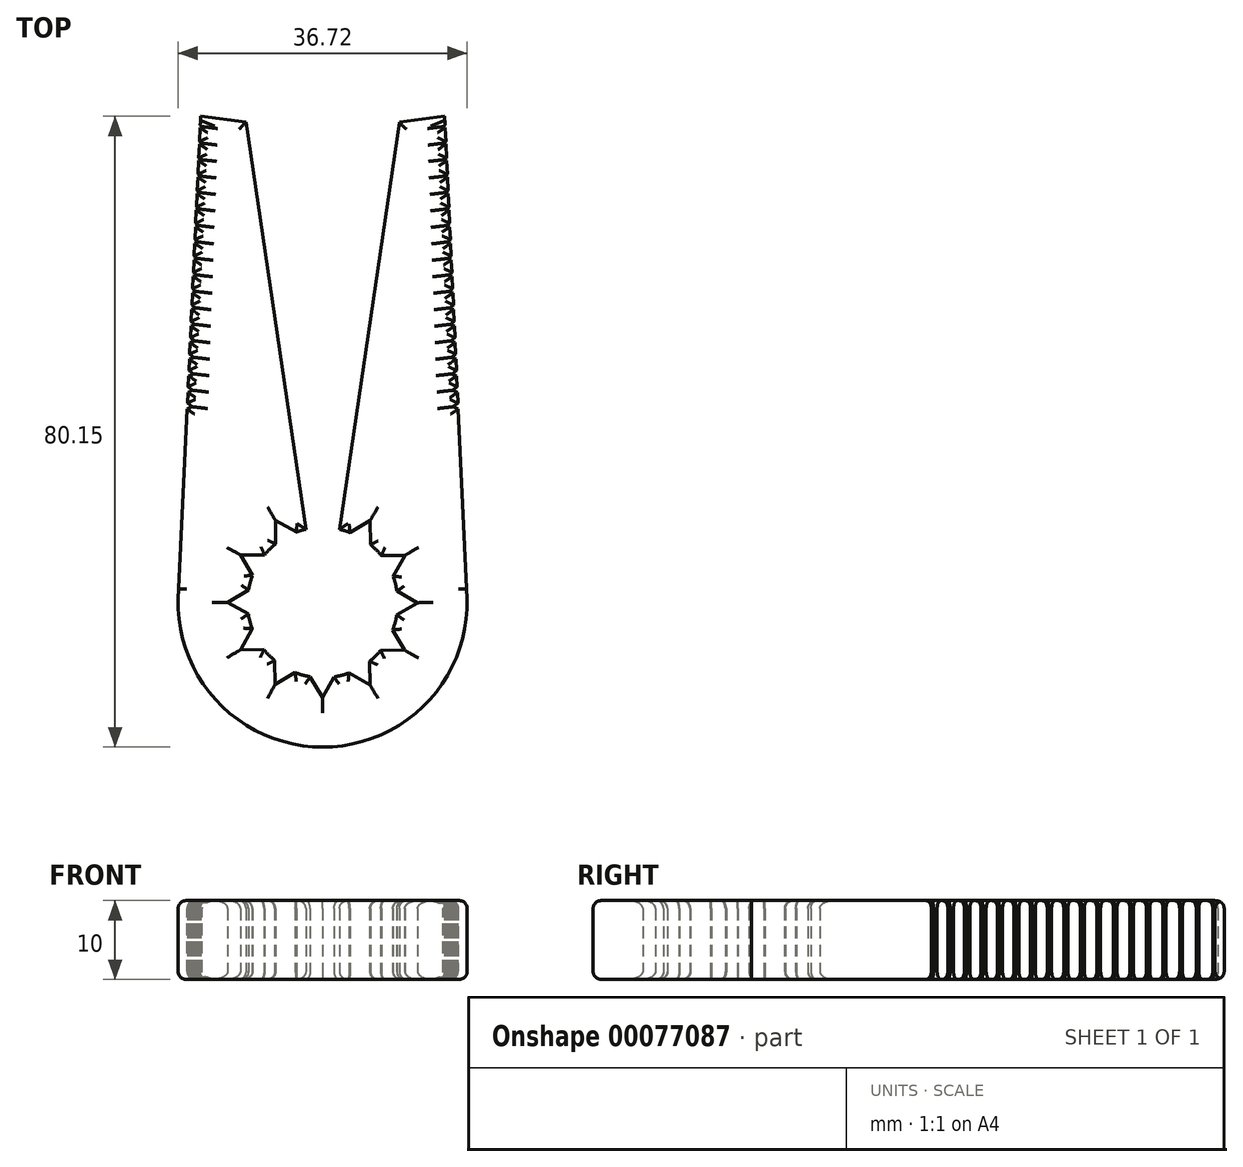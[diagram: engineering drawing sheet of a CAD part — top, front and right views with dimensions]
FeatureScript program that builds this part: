
annotation { "Feature Type Name" : "Feature", "Feature Type Description" : "" }
export const myFeature = defineFeature(function(context is Context, id is Id, definition is map)
    precondition{}
    {
        {
            var Q0;
            Q0=qCreatedBy(makeId("Top.planeOp"),FACE);
            var sketch = newSketch(context, id + "F0", { "sketchPlane" : qUnion([Q0])});
            skLineSegment(sketch, "E0", {"start": v(-9.75, 60.98) * mm, "end": v(-15.5, 61.76) * mm});
            skLineSegment(sketch, "E1", {"start": v(-15.5, 61.76) * mm, "end": v(-16.2, 46.6) * mm});
            skLineSegment(sketch, "E2", {"start": v(0, 52.98) * mm, "end": v(0, 8.77) * mm, "construction": true});
            skArc(sketch, "E3.trimOffspring", {"start": v(-18.28, 1.74) * mm, "mid": v(-13.6, -12.37) * mm, "end": v(0, -18.4) * mm});
            skArc(sketch, "E4.MirrorCS", {"start": v(18.28, 1.74) * mm, "mid": v(13.6, -12.37) * mm, "end": v(0, -18.4) * mm});
            skLineSegment(sketch, "E5.MirrorCS", {"start": v(15.5, 61.76) * mm, "end": v(16.2, 46.6) * mm});
            skLineSegment(sketch, "E6.MirrorCS", {"start": v(9.75, 60.98) * mm, "end": v(15.5, 61.76) * mm});
            skLineSegment(sketch, "E7.MirrorCS", {"start": v(2.13, 9.28) * mm, "end": v(9.75, 60.98) * mm});
            skLineSegment(sketch, "E8.trimOffspring", {"start": v(-16.76, 34.47) * mm, "end": v(-18.28, 1.74) * mm});
            skLineSegment(sketch, "E9.trimOffspring", {"start": v(16.76, 34.47) * mm, "end": v(18.28, 1.74) * mm});
            skLineSegment(sketch, "E10", {"start": v(-2.13, 9.28) * mm, "end": v(-9.75, 60.98) * mm});
            skLineSegment(sketch, "E11.trimOffspring", {"start": v(0, 8.03) * mm, "end": v(0, -53.52) * mm, "construction": true});
            skArc(sketch, "E12", {"start": v(-2.13, 9.28) * mm, "mid": v(-2.74, 9.12) * mm, "end": v(-3.34, 8.92) * mm});
            skLineSegment(sketch, "E13", {"start": v(0, -0.03) * mm, "end": v(-26.83, -0.03) * mm, "construction": true});
            skArc(sketch, "E14.cCircle", {"start": v(-7.66, -0.03) * mm, "mid": v(-7.66, 0) * mm, "end": v(-7.66, 0.04) * mm, "construction": true});
            skLineSegment(sketch, "E14.0", {"start": v(-12.05, 0) * mm, "end": v(-9.42, 1.55) * mm});
            skLineSegment(sketch, "E14.1", {"start": v(-7.66, 0.04) * mm, "end": v(-7.66, -0.03) * mm});
            skLineSegment(sketch, "E14.2", {"start": v(-9.44, -1.47) * mm, "end": v(-12.05, 0) * mm});
            skPoint(sketch, "E14.0.midPoint", {"position": v(-9.87, 1.28) * mm});
            skPoint(sketch, "E15.orphan", {"position": v(-7.69, 2.57) * mm});
            skPoint(sketch, "E16.orphan", {"position": v(-7.63, -2.49) * mm});
            skPoint(sketch, "E17.1.0", {"position": v(-9.2, -3.83) * mm});
            skLineSegment(sketch, "E17.1.1", {"start": v(-10.44, -6.03) * mm, "end": v(-8.95, -3.37) * mm});
            skLineSegment(sketch, "E17.1.2", {"start": v(-7.45, -6) * mm, "end": v(-10.44, -6.03) * mm});
            skPoint(sketch, "E17.2.0", {"position": v(-6.07, -7.92) * mm});
            skLineSegment(sketch, "E17.2.1", {"start": v(-6.04, -10.45) * mm, "end": v(-6.08, -7.4) * mm});
            skLineSegment(sketch, "E17.2.2", {"start": v(-3.47, -8.93) * mm, "end": v(-6.04, -10.45) * mm});
            skPoint(sketch, "E17.3.0", {"position": v(-1.31, -9.9) * mm});
            skLineSegment(sketch, "E17.3.1", {"start": v(-0.02, -12.08) * mm, "end": v(-1.58, -9.45) * mm});
            skLineSegment(sketch, "E17.3.2", {"start": v(1.44, -9.47) * mm, "end": v(-0.02, -12.08) * mm});
            skPoint(sketch, "E17.4.0", {"position": v(3.8, -9.23) * mm});
            skLineSegment(sketch, "E17.4.1", {"start": v(6, -10.47) * mm, "end": v(3.34, -8.97) * mm});
            skLineSegment(sketch, "E17.4.2", {"start": v(5.97, -7.48) * mm, "end": v(6, -10.47) * mm});
            skPoint(sketch, "E17.5.0", {"position": v(7.9, -6.1) * mm});
            skLineSegment(sketch, "E17.5.1", {"start": v(10.42, -6.07) * mm, "end": v(7.37, -6.1) * mm});
            skLineSegment(sketch, "E17.5.2", {"start": v(8.9, -3.5) * mm, "end": v(10.42, -6.07) * mm});
            skPoint(sketch, "E17.6.0", {"position": v(9.87, -1.34) * mm});
            skLineSegment(sketch, "E17.6.1", {"start": v(12.05, -0.05) * mm, "end": v(9.42, -1.6) * mm});
            skLineSegment(sketch, "E17.6.2", {"start": v(9.44, 1.42) * mm, "end": v(12.05, -0.05) * mm});
            skPoint(sketch, "E17.7.0", {"position": v(9.2, 3.77) * mm});
            skLineSegment(sketch, "E17.7.1", {"start": v(10.44, 5.98) * mm, "end": v(8.95, 3.31) * mm});
            skLineSegment(sketch, "E17.7.2", {"start": v(7.45, 5.94) * mm, "end": v(10.44, 5.98) * mm});
            skPoint(sketch, "E17.8.0", {"position": v(6.07, 7.86) * mm});
            skLineSegment(sketch, "E17.8.1", {"start": v(6.04, 10.4) * mm, "end": v(6.08, 7.34) * mm});
            skLineSegment(sketch, "E17.8.2", {"start": v(3.47, 8.87) * mm, "end": v(6.04, 10.4) * mm});
            skPoint(sketch, "E17.9.0", {"position": v(1.31, 9.84) * mm});
            skLineSegment(sketch, "E17.9.1", {"start": v(0, 12.05) * mm, "end": v(0.02, 12.02) * mm});
            skPoint(sketch, "E17.10.0", {"position": v(-3.8, 9.17) * mm});
            skLineSegment(sketch, "E17.10.1", {"start": v(-6, 10.42) * mm, "end": v(-3.34, 8.92) * mm});
            skLineSegment(sketch, "E17.10.2", {"start": v(-5.97, 7.42) * mm, "end": v(-6, 10.42) * mm});
            skPoint(sketch, "E17.11.0", {"position": v(-7.9, 6.04) * mm});
            skLineSegment(sketch, "E17.11.1", {"start": v(-10.42, 6.01) * mm, "end": v(-7.37, 6.05) * mm});
            skLineSegment(sketch, "E17.11.2", {"start": v(-8.9, 3.44) * mm, "end": v(-10.42, 6.01) * mm});
            skArc(sketch, "E18.trimOffspring", {"start": v(3.47, 8.87) * mm, "mid": v(2.8, 9.1) * mm, "end": v(2.13, 9.28) * mm});
            skArc(sketch, "E19.trimOffspring", {"start": v(7.45, 5.94) * mm, "mid": v(6.8, 6.68) * mm, "end": v(6.08, 7.34) * mm});
            skArc(sketch, "E20.trimOffspring", {"start": v(9.44, 1.42) * mm, "mid": v(9.24, 2.38) * mm, "end": v(8.95, 3.31) * mm});
            skArc(sketch, "E21.trimOffspring", {"start": v(8.9, -3.5) * mm, "mid": v(9.2, -2.57) * mm, "end": v(9.42, -1.6) * mm});
            skArc(sketch, "E22.trimOffspring", {"start": v(5.97, -7.48) * mm, "mid": v(6.7, -6.83) * mm, "end": v(7.37, -6.1) * mm});
            skArc(sketch, "E23.trimOffspring", {"start": v(1.44, -9.47) * mm, "mid": v(2.4, -9.27) * mm, "end": v(3.34, -8.97) * mm});
            skArc(sketch, "E24.trimOffspring", {"start": v(-3.47, -8.93) * mm, "mid": v(-2.54, -9.24) * mm, "end": v(-1.58, -9.45) * mm});
            skArc(sketch, "E25.trimOffspring", {"start": v(-7.45, -6) * mm, "mid": v(-6.8, -6.73) * mm, "end": v(-6.08, -7.4) * mm});
            skArc(sketch, "E26.trimOffspring", {"start": v(-9.44, -1.47) * mm, "mid": v(-9.24, -2.43) * mm, "end": v(-8.95, -3.37) * mm});
            skArc(sketch, "E27.trimOffspring", {"start": v(-8.9, 3.44) * mm, "mid": v(-9.2, 2.5) * mm, "end": v(-9.42, 1.55) * mm});
            skArc(sketch, "E28.trimOffspring", {"start": v(-5.97, 7.42) * mm, "mid": v(-6.7, 6.77) * mm, "end": v(-7.37, 6.05) * mm});
            skLineSegment(sketch, "E29", {"start": v(-16.2, 46.6) * mm, "end": v(-16.76, 34.47) * mm});
            skLineSegment(sketch, "E30", {"start": v(16.2, 46.6) * mm, "end": v(16.76, 34.47) * mm});
            skSolve(sketch);
        }
        {
            var Q0;
            Q0=makeQuery(id+"F0.imprint","IMPRINT",FACE,{"disambiguationData":[TD([[makeQuery(id+"F0.imprint","IMPRINT",EDGE,{"derivedFrom":sQuery(id+"F0.wireOp",EDGE,"E0")}),1.0]])]});
            extrude(context, id + "F1", {"entities" : qUnion([Q0]), "depth" : 10 * mm});
        }
        {
            var Q0;
            Q0=qCreatedBy(makeId("Top.planeOp"),FACE);
            var sketch = newSketch(context, id + "F2", { "sketchPlane" : qUnion([Q0])});
            skLineSegment(sketch, "E31.0", {"start": v(-16.57, 24.85) * mm, "end": v(-25.04, 21.22) * mm});
            skLineSegment(sketch, "E31.1", {"start": v(-25.04, 21.22) * mm, "end": v(-23.95, 30.36) * mm});
            skLineSegment(sketch, "E31.2", {"start": v(-23.95, 30.36) * mm, "end": v(-16.57, 24.85) * mm});
            skPoint(sketch, "E31.0.midPoint", {"position": v(-20.8, 23.03) * mm});
            skLineSegment(sketch, "E32.1.0.0", {"start": v(-24.96, 23.31) * mm, "end": v(-23.87, 32.46) * mm});
            skPoint(sketch, "E32.1.0.1", {"position": v(-20.73, 25.13) * mm});
            skLineSegment(sketch, "E32.1.0.2", {"start": v(-23.87, 32.46) * mm, "end": v(-16.5, 26.94) * mm});
            skLineSegment(sketch, "E32.1.0.3", {"start": v(-16.5, 26.94) * mm, "end": v(-24.96, 23.31) * mm});
            skLineSegment(sketch, "E32.2.0.0", {"start": v(-24.89, 25.4) * mm, "end": v(-23.8, 34.55) * mm});
            skPoint(sketch, "E32.2.0.1", {"position": v(-20.66, 27.22) * mm});
            skLineSegment(sketch, "E32.2.0.2", {"start": v(-23.8, 34.55) * mm, "end": v(-16.42, 29.03) * mm});
            skLineSegment(sketch, "E32.2.0.3", {"start": v(-16.42, 29.03) * mm, "end": v(-24.89, 25.4) * mm});
            skLineSegment(sketch, "E32.3.0.0", {"start": v(-24.81, 27.5) * mm, "end": v(-23.72, 36.64) * mm});
            skPoint(sketch, "E32.3.0.1", {"position": v(-20.58, 29.31) * mm});
            skLineSegment(sketch, "E32.3.0.2", {"start": v(-23.72, 36.64) * mm, "end": v(-16.35, 31.13) * mm});
            skLineSegment(sketch, "E32.3.0.3", {"start": v(-16.35, 31.13) * mm, "end": v(-24.81, 27.5) * mm});
            skLineSegment(sketch, "E32.4.0.0", {"start": v(-24.74, 29.6) * mm, "end": v(-23.65, 38.74) * mm});
            skPoint(sketch, "E32.4.0.1", {"position": v(-20.5, 31.4) * mm});
            skLineSegment(sketch, "E32.4.0.2", {"start": v(-23.65, 38.74) * mm, "end": v(-16.27, 33.22) * mm});
            skLineSegment(sketch, "E32.4.0.3", {"start": v(-16.27, 33.22) * mm, "end": v(-24.74, 29.6) * mm});
            skLineSegment(sketch, "E32.5.0.0", {"start": v(-24.66, 31.69) * mm, "end": v(-23.57, 40.83) * mm});
            skPoint(sketch, "E32.5.0.1", {"position": v(-20.43, 33.5) * mm});
            skLineSegment(sketch, "E32.5.0.2", {"start": v(-23.57, 40.83) * mm, "end": v(-16.2, 35.31) * mm});
            skLineSegment(sketch, "E32.5.0.3", {"start": v(-16.2, 35.31) * mm, "end": v(-24.66, 31.69) * mm});
            skLineSegment(sketch, "E32.6.0.0", {"start": v(-24.59, 33.78) * mm, "end": v(-23.5, 42.92) * mm});
            skPoint(sketch, "E32.6.0.1", {"position": v(-20.36, 35.6) * mm});
            skLineSegment(sketch, "E32.6.0.2", {"start": v(-23.5, 42.92) * mm, "end": v(-16.12, 37.4) * mm});
            skLineSegment(sketch, "E32.6.0.3", {"start": v(-16.12, 37.4) * mm, "end": v(-24.59, 33.78) * mm});
            skLineSegment(sketch, "E32.7.0.0", {"start": v(-24.51, 35.87) * mm, "end": v(-23.42, 45.02) * mm});
            skPoint(sketch, "E32.7.0.1", {"position": v(-20.28, 37.69) * mm});
            skLineSegment(sketch, "E32.7.0.2", {"start": v(-23.42, 45.02) * mm, "end": v(-16.05, 39.5) * mm});
            skLineSegment(sketch, "E32.7.0.3", {"start": v(-16.05, 39.5) * mm, "end": v(-24.51, 35.87) * mm});
            skLineSegment(sketch, "E32.8.0.0", {"start": v(-24.44, 37.97) * mm, "end": v(-23.35, 47.1) * mm});
            skPoint(sketch, "E32.8.0.1", {"position": v(-20.2, 39.78) * mm});
            skLineSegment(sketch, "E32.8.0.2", {"start": v(-23.35, 47.1) * mm, "end": v(-15.98, 41.6) * mm});
            skLineSegment(sketch, "E32.8.0.3", {"start": v(-15.98, 41.6) * mm, "end": v(-24.44, 37.97) * mm});
            skLineSegment(sketch, "E32.9.0.0", {"start": v(-24.36, 40.06) * mm, "end": v(-23.27, 49.2) * mm});
            skPoint(sketch, "E32.9.0.1", {"position": v(-20.13, 41.87) * mm});
            skLineSegment(sketch, "E32.9.0.2", {"start": v(-23.27, 49.2) * mm, "end": v(-15.9, 43.69) * mm});
            skLineSegment(sketch, "E32.9.0.3", {"start": v(-15.9, 43.69) * mm, "end": v(-24.36, 40.06) * mm});
            skLineSegment(sketch, "E32.10.0.0", {"start": v(-24.29, 42.15) * mm, "end": v(-23.2, 51.3) * mm});
            skPoint(sketch, "E32.10.0.1", {"position": v(-20.06, 43.97) * mm});
            skLineSegment(sketch, "E32.10.0.2", {"start": v(-23.2, 51.3) * mm, "end": v(-15.83, 45.78) * mm});
            skLineSegment(sketch, "E32.10.0.3", {"start": v(-15.83, 45.78) * mm, "end": v(-24.29, 42.15) * mm});
            skLineSegment(sketch, "E32.11.0.0", {"start": v(-24.21, 44.25) * mm, "end": v(-23.12, 53.39) * mm});
            skPoint(sketch, "E32.11.0.1", {"position": v(-19.98, 46.06) * mm});
            skLineSegment(sketch, "E32.11.0.2", {"start": v(-23.12, 53.39) * mm, "end": v(-15.75, 47.87) * mm});
            skLineSegment(sketch, "E32.11.0.3", {"start": v(-15.75, 47.87) * mm, "end": v(-24.21, 44.25) * mm});
            skLineSegment(sketch, "E32.12.0.0", {"start": v(-24.14, 46.34) * mm, "end": v(-23.05, 55.48) * mm});
            skPoint(sketch, "E32.12.0.1", {"position": v(-19.9, 48.15) * mm});
            skLineSegment(sketch, "E32.12.0.2", {"start": v(-23.05, 55.48) * mm, "end": v(-15.68, 49.97) * mm});
            skLineSegment(sketch, "E32.12.0.3", {"start": v(-15.68, 49.97) * mm, "end": v(-24.14, 46.34) * mm});
            skLineSegment(sketch, "E32.13.0.0", {"start": v(-24.06, 48.43) * mm, "end": v(-22.97, 57.57) * mm});
            skPoint(sketch, "E32.13.0.1", {"position": v(-19.83, 50.25) * mm});
            skLineSegment(sketch, "E32.13.0.2", {"start": v(-22.97, 57.57) * mm, "end": v(-15.6, 52.06) * mm});
            skLineSegment(sketch, "E32.13.0.3", {"start": v(-15.6, 52.06) * mm, "end": v(-24.06, 48.43) * mm});
            skLineSegment(sketch, "E32.14.0.0", {"start": v(-23.99, 50.53) * mm, "end": v(-22.9, 59.67) * mm});
            skPoint(sketch, "E32.14.0.1", {"position": v(-19.76, 52.34) * mm});
            skLineSegment(sketch, "E32.14.0.2", {"start": v(-22.9, 59.67) * mm, "end": v(-15.53, 54.15) * mm});
            skLineSegment(sketch, "E32.14.0.3", {"start": v(-15.53, 54.15) * mm, "end": v(-23.99, 50.53) * mm});
            skLineSegment(sketch, "E32.15.0.0", {"start": v(-23.91, 52.62) * mm, "end": v(-22.82, 61.76) * mm});
            skPoint(sketch, "E32.15.0.1", {"position": v(-19.68, 54.43) * mm});
            skLineSegment(sketch, "E32.15.0.2", {"start": v(-22.82, 61.76) * mm, "end": v(-15.45, 56.25) * mm});
            skLineSegment(sketch, "E32.15.0.3", {"start": v(-15.45, 56.25) * mm, "end": v(-23.91, 52.62) * mm});
            skLineSegment(sketch, "E32.16.0.0", {"start": v(-23.84, 54.71) * mm, "end": v(-22.75, 63.85) * mm});
            skPoint(sketch, "E32.16.0.1", {"position": v(-19.6, 56.53) * mm});
            skLineSegment(sketch, "E32.16.0.2", {"start": v(-22.75, 63.85) * mm, "end": v(-15.38, 58.34) * mm});
            skLineSegment(sketch, "E32.16.0.3", {"start": v(-15.38, 58.34) * mm, "end": v(-23.84, 54.71) * mm});
            skLineSegment(sketch, "E32.17.0.0", {"start": v(-23.76, 56.8) * mm, "end": v(-22.67, 65.95) * mm});
            skPoint(sketch, "E32.17.0.1", {"position": v(-19.53, 58.62) * mm});
            skLineSegment(sketch, "E32.17.0.2", {"start": v(-22.67, 65.95) * mm, "end": v(-15.3, 60.43) * mm});
            skLineSegment(sketch, "E32.17.0.3", {"start": v(-15.3, 60.43) * mm, "end": v(-23.76, 56.8) * mm});
            skLineSegment(sketch, "E32.direction1", {"start": v(-25.04, 21.22) * mm, "end": v(-24.96, 23.31) * mm, "construction": true});
            skLineSegment(sketch, "E33", {"start": v(0, 70.25) * mm, "end": v(0, -30.92) * mm, "construction": true});
            skLineSegment(sketch, "E34.MirrorCS", {"start": v(25.04, 21.22) * mm, "end": v(24.96, 23.31) * mm, "construction": true});
            skLineSegment(sketch, "E35.MirrorCS", {"start": v(24.36, 40.06) * mm, "end": v(23.27, 49.2) * mm});
            skLineSegment(sketch, "E36.MirrorCS", {"start": v(24.51, 35.87) * mm, "end": v(23.42, 45.02) * mm});
            skLineSegment(sketch, "E37.MirrorCS", {"start": v(23.76, 56.8) * mm, "end": v(22.67, 65.95) * mm});
            skLineSegment(sketch, "E38.MirrorCS", {"start": v(24.66, 31.69) * mm, "end": v(23.57, 40.83) * mm});
            skLineSegment(sketch, "E39.MirrorCS", {"start": v(24.44, 37.97) * mm, "end": v(23.35, 47.1) * mm});
            skLineSegment(sketch, "E40.MirrorCS", {"start": v(25.04, 21.22) * mm, "end": v(23.95, 30.36) * mm});
            skLineSegment(sketch, "E41.MirrorCS", {"start": v(23.99, 50.53) * mm, "end": v(22.9, 59.67) * mm});
            skLineSegment(sketch, "E42.MirrorCS", {"start": v(24.81, 27.5) * mm, "end": v(23.72, 36.64) * mm});
            skLineSegment(sketch, "E43.MirrorCS", {"start": v(24.29, 42.15) * mm, "end": v(23.2, 51.3) * mm});
            skLineSegment(sketch, "E44.MirrorCS", {"start": v(24.21, 44.25) * mm, "end": v(23.12, 53.39) * mm});
            skLineSegment(sketch, "E45.MirrorCS", {"start": v(24.89, 25.4) * mm, "end": v(23.8, 34.55) * mm});
            skLineSegment(sketch, "E46.MirrorCS", {"start": v(23.84, 54.71) * mm, "end": v(22.75, 63.85) * mm});
            skLineSegment(sketch, "E47.MirrorCS", {"start": v(24.14, 46.34) * mm, "end": v(23.05, 55.48) * mm});
            skLineSegment(sketch, "E48.MirrorCS", {"start": v(24.96, 23.31) * mm, "end": v(23.87, 32.46) * mm});
            skLineSegment(sketch, "E49.MirrorCS", {"start": v(24.59, 33.78) * mm, "end": v(23.5, 42.92) * mm});
            skLineSegment(sketch, "E50.MirrorCS", {"start": v(23.91, 52.62) * mm, "end": v(22.82, 61.76) * mm});
            skLineSegment(sketch, "E51.MirrorCS", {"start": v(24.74, 29.6) * mm, "end": v(23.65, 38.74) * mm});
            skLineSegment(sketch, "E52.MirrorCS", {"start": v(24.06, 48.43) * mm, "end": v(22.97, 57.57) * mm});
            skLineSegment(sketch, "E53.MirrorCS", {"start": v(22.9, 59.67) * mm, "end": v(15.53, 54.15) * mm});
            skLineSegment(sketch, "E54.MirrorCS", {"start": v(23.95, 30.36) * mm, "end": v(16.57, 24.85) * mm});
            skLineSegment(sketch, "E55.MirrorCS", {"start": v(15.53, 54.15) * mm, "end": v(23.99, 50.53) * mm});
            skLineSegment(sketch, "E56.MirrorCS", {"start": v(16.27, 33.22) * mm, "end": v(24.74, 29.6) * mm});
            skLineSegment(sketch, "E57.MirrorCS", {"start": v(23.57, 40.83) * mm, "end": v(16.2, 35.31) * mm});
            skLineSegment(sketch, "E58.MirrorCS", {"start": v(23.42, 45.02) * mm, "end": v(16.05, 39.5) * mm});
            skLineSegment(sketch, "E59.MirrorCS", {"start": v(23.5, 42.92) * mm, "end": v(16.12, 37.4) * mm});
            skLineSegment(sketch, "E60.MirrorCS", {"start": v(23.12, 53.39) * mm, "end": v(15.75, 47.87) * mm});
            skLineSegment(sketch, "E61.MirrorCS", {"start": v(15.3, 60.43) * mm, "end": v(23.76, 56.8) * mm});
            skPoint(sketch, "E62.MirrorP", {"position": v(19.83, 50.25) * mm});
            skLineSegment(sketch, "E63.MirrorCS", {"start": v(23.05, 55.48) * mm, "end": v(15.68, 49.97) * mm});
            skPoint(sketch, "E64.MirrorP", {"position": v(20.43, 33.5) * mm});
            skLineSegment(sketch, "E65.MirrorCS", {"start": v(22.67, 65.95) * mm, "end": v(15.3, 60.43) * mm});
            skLineSegment(sketch, "E66.MirrorCS", {"start": v(16.12, 37.4) * mm, "end": v(24.59, 33.78) * mm});
            skLineSegment(sketch, "E67.MirrorCS", {"start": v(16.5, 26.94) * mm, "end": v(24.96, 23.31) * mm});
            skLineSegment(sketch, "E68.MirrorCS", {"start": v(23.87, 32.46) * mm, "end": v(16.5, 26.94) * mm});
            skLineSegment(sketch, "E69.MirrorCS", {"start": v(16.57, 24.85) * mm, "end": v(25.04, 21.22) * mm});
            skPoint(sketch, "E70.MirrorP", {"position": v(19.76, 52.34) * mm});
            skLineSegment(sketch, "E71.MirrorCS", {"start": v(23.27, 49.2) * mm, "end": v(15.9, 43.69) * mm});
            skLineSegment(sketch, "E72.MirrorCS", {"start": v(23.65, 38.74) * mm, "end": v(16.27, 33.22) * mm});
            skPoint(sketch, "E73.MirrorP", {"position": v(20.2, 39.78) * mm});
            skLineSegment(sketch, "E74.MirrorCS", {"start": v(22.97, 57.57) * mm, "end": v(15.6, 52.06) * mm});
            skPoint(sketch, "E75.MirrorP", {"position": v(20.28, 37.69) * mm});
            skPoint(sketch, "E76.MirrorP", {"position": v(20.36, 35.6) * mm});
            skLineSegment(sketch, "E77.MirrorCS", {"start": v(15.98, 41.6) * mm, "end": v(24.44, 37.97) * mm});
            skPoint(sketch, "E78.MirrorP", {"position": v(20.5, 31.4) * mm});
            skLineSegment(sketch, "E79.MirrorCS", {"start": v(16.35, 31.13) * mm, "end": v(24.81, 27.5) * mm});
            skPoint(sketch, "E80.MirrorP", {"position": v(20.58, 29.31) * mm});
            skLineSegment(sketch, "E81.MirrorCS", {"start": v(22.82, 61.76) * mm, "end": v(15.45, 56.25) * mm});
            skPoint(sketch, "E82.MirrorP", {"position": v(19.53, 58.62) * mm});
            skPoint(sketch, "E83.MirrorP", {"position": v(19.9, 48.15) * mm});
            skPoint(sketch, "E84.MirrorP", {"position": v(20.73, 25.13) * mm});
            skLineSegment(sketch, "E85.MirrorCS", {"start": v(16.2, 35.31) * mm, "end": v(24.66, 31.69) * mm});
            skLineSegment(sketch, "E86.MirrorCS", {"start": v(15.38, 58.34) * mm, "end": v(23.84, 54.71) * mm});
            skLineSegment(sketch, "E87.MirrorCS", {"start": v(23.72, 36.64) * mm, "end": v(16.35, 31.13) * mm});
            skPoint(sketch, "E88.MirrorP", {"position": v(19.68, 54.43) * mm});
            skLineSegment(sketch, "E89.MirrorCS", {"start": v(15.68, 49.97) * mm, "end": v(24.14, 46.34) * mm});
            skLineSegment(sketch, "E90.MirrorCS", {"start": v(23.2, 51.3) * mm, "end": v(15.83, 45.78) * mm});
            skPoint(sketch, "E91.MirrorP", {"position": v(19.6, 56.53) * mm});
            skPoint(sketch, "E92.MirrorP", {"position": v(20.8, 23.03) * mm});
            skLineSegment(sketch, "E93.MirrorCS", {"start": v(15.83, 45.78) * mm, "end": v(24.29, 42.15) * mm});
            skPoint(sketch, "E94.MirrorP", {"position": v(20.13, 41.87) * mm});
            skLineSegment(sketch, "E95.MirrorCS", {"start": v(16.42, 29.03) * mm, "end": v(24.89, 25.4) * mm});
            skLineSegment(sketch, "E96.MirrorCS", {"start": v(23.8, 34.55) * mm, "end": v(16.42, 29.03) * mm});
            skPoint(sketch, "E97.MirrorP", {"position": v(20.06, 43.97) * mm});
            skPoint(sketch, "E98.MirrorP", {"position": v(20.66, 27.22) * mm});
            skPoint(sketch, "E99.MirrorP", {"position": v(19.98, 46.06) * mm});
            skLineSegment(sketch, "E100.MirrorCS", {"start": v(15.9, 43.69) * mm, "end": v(24.36, 40.06) * mm});
            skLineSegment(sketch, "E101.MirrorCS", {"start": v(23.35, 47.1) * mm, "end": v(15.98, 41.6) * mm});
            skLineSegment(sketch, "E102.MirrorCS", {"start": v(15.45, 56.25) * mm, "end": v(23.91, 52.62) * mm});
            skLineSegment(sketch, "E103.MirrorCS", {"start": v(15.75, 47.87) * mm, "end": v(24.21, 44.25) * mm});
            skLineSegment(sketch, "E104.MirrorCS", {"start": v(22.75, 63.85) * mm, "end": v(15.38, 58.34) * mm});
            skLineSegment(sketch, "E105.MirrorCS", {"start": v(15.6, 52.06) * mm, "end": v(24.06, 48.43) * mm});
            skLineSegment(sketch, "E106.MirrorCS", {"start": v(16.05, 39.5) * mm, "end": v(24.51, 35.87) * mm});
            skSolve(sketch);
        }
        {
            var Q0;
            {var subQ5=sQuery(id+"F2.wireOp",EDGE,"E32.15.0.2");var subQ6=sQuery(id+"F2.wireOp",EDGE,"E32.15.0.0");var subQ7=makeQuery(id+"F2.imprint","INTERSECT",VERTEX,{"derivedFrom":[subQ6,subQ5]});Q0=makeQuery(id+"F2.imprint","IMPRINT",FACE,{"disambiguationData":[TD([[makeQuery(id+"F2.imprint","IMPRINT",EDGE,{"disambiguationData":[TD([[subQ7,1.0]])],"derivedFrom":subQ6}),1.0]])]});}
            var Q1;
            {var subQ0=sQuery(id+"F2.wireOp",EDGE,"E32.6.0.3");var subQ1=sQuery(id+"F2.wireOp",EDGE,"E32.5.0.2");var subQ2=makeQuery(id+"F2.imprint","INTERSECT",VERTEX,{"derivedFrom":[subQ1,subQ0]});Q1=makeQuery(id+"F2.imprint","IMPRINT",FACE,{"disambiguationData":[TD([[makeQuery(id+"F2.imprint","IMPRINT",EDGE,{"disambiguationData":[TD([[subQ2,1.0]])],"derivedFrom":subQ1}),1.0]])]});}
            var Q2;
            {var subQ0=sQuery(id+"F2.wireOp",EDGE,"E32.16.0.3");var subQ1=sQuery(id+"F2.wireOp",EDGE,"E32.15.0.2");var subQ2=makeQuery(id+"F2.imprint","INTERSECT",VERTEX,{"derivedFrom":[subQ1,subQ0]});Q2=makeQuery(id+"F2.imprint","IMPRINT",FACE,{"disambiguationData":[TD([[makeQuery(id+"F2.imprint","IMPRINT",EDGE,{"disambiguationData":[TD([[subQ2,1.0]])],"derivedFrom":subQ1}),1.0]])]});}
            var Q3;
            {var subQ0=sQuery(id+"F2.wireOp",EDGE,"E32.1.0.3");var subQ1=sQuery(id+"F2.wireOp",EDGE,"E31.1");var subQ2=makeQuery(id+"F2.imprint","INTERSECT",VERTEX,{"derivedFrom":[subQ1,subQ0]});Q3=makeQuery(id+"F2.imprint","IMPRINT",FACE,{"disambiguationData":[TD([[makeQuery(id+"F2.imprint","IMPRINT",EDGE,{"disambiguationData":[TD([[subQ2,-1.0]])],"derivedFrom":subQ1}),-1.0]])]});}
            var Q4;
            {var subQ0=sQuery(id+"F2.wireOp",EDGE,"E32.2.0.3");var subQ1=sQuery(id+"F2.wireOp",EDGE,"E31.1");var subQ2=makeQuery(id+"F2.imprint","INTERSECT",VERTEX,{"derivedFrom":[subQ1,subQ0]});Q4=makeQuery(id+"F2.imprint","IMPRINT",FACE,{"disambiguationData":[TD([[makeQuery(id+"F2.imprint","IMPRINT",EDGE,{"disambiguationData":[TD([[subQ2,-1.0]])],"derivedFrom":subQ1}),-1.0]])]});}
            var Q5;
            {var subQ0=sQuery(id+"F2.wireOp",EDGE,"E32.14.0.3");var subQ1=sQuery(id+"F2.wireOp",EDGE,"E32.13.0.2");var subQ2=makeQuery(id+"F2.imprint","INTERSECT",VERTEX,{"derivedFrom":[subQ1,subQ0]});Q5=makeQuery(id+"F2.imprint","IMPRINT",FACE,{"disambiguationData":[TD([[makeQuery(id+"F2.imprint","IMPRINT",EDGE,{"disambiguationData":[TD([[subQ2,1.0]])],"derivedFrom":subQ1}),1.0]])]});}
            var Q6;
            {var subQ0=sQuery(id+"F2.wireOp",EDGE,"E32.7.0.3");var subQ1=sQuery(id+"F2.wireOp",EDGE,"E32.6.0.2");var subQ2=makeQuery(id+"F2.imprint","INTERSECT",VERTEX,{"derivedFrom":[subQ1,subQ0]});Q6=makeQuery(id+"F2.imprint","IMPRINT",FACE,{"disambiguationData":[TD([[makeQuery(id+"F2.imprint","IMPRINT",EDGE,{"disambiguationData":[TD([[subQ2,1.0]])],"derivedFrom":subQ1}),1.0]])]});}
            var Q7;
            {var subQ0=sQuery(id+"F2.wireOp",EDGE,"E32.13.0.3");var subQ1=sQuery(id+"F2.wireOp",EDGE,"E32.12.0.2");var subQ2=makeQuery(id+"F2.imprint","INTERSECT",VERTEX,{"derivedFrom":[subQ1,subQ0]});Q7=makeQuery(id+"F2.imprint","IMPRINT",FACE,{"disambiguationData":[TD([[makeQuery(id+"F2.imprint","IMPRINT",EDGE,{"disambiguationData":[TD([[subQ2,1.0]])],"derivedFrom":subQ1}),1.0]])]});}
            var Q8;
            {var subQ0=sQuery(id+"F2.wireOp",EDGE,"E32.4.0.3");var subQ1=sQuery(id+"F2.wireOp",EDGE,"E32.3.0.2");var subQ2=makeQuery(id+"F2.imprint","INTERSECT",VERTEX,{"derivedFrom":[subQ1,subQ0]});Q8=makeQuery(id+"F2.imprint","IMPRINT",FACE,{"disambiguationData":[TD([[makeQuery(id+"F2.imprint","IMPRINT",EDGE,{"disambiguationData":[TD([[subQ2,1.0]])],"derivedFrom":subQ1}),1.0]])]});}
            var Q9;
            {var subQ1=sQuery(id+"F2.wireOp",EDGE,"E32.17.0.0");Q9=makeQuery(id+"F2.imprint","IMPRINT",FACE,{"disambiguationData":[TD([[makeQuery(id+"F2.imprint","IMPRINT",EDGE,{"derivedFrom":subQ1}),-1.0]])]});}
            var Q10;
            {var subQ0=sQuery(id+"F2.wireOp",EDGE,"E32.3.0.3");var subQ1=sQuery(id+"F2.wireOp",EDGE,"E32.2.0.2");var subQ2=makeQuery(id+"F2.imprint","INTERSECT",VERTEX,{"derivedFrom":[subQ1,subQ0]});Q10=makeQuery(id+"F2.imprint","IMPRINT",FACE,{"disambiguationData":[TD([[makeQuery(id+"F2.imprint","IMPRINT",EDGE,{"disambiguationData":[TD([[subQ2,1.0]])],"derivedFrom":subQ1}),1.0]])]});}
            var Q11;
            {var subQ0=sQuery(id+"F2.wireOp",EDGE,"E32.15.0.3");var subQ1=sQuery(id+"F2.wireOp",EDGE,"E32.14.0.2");var subQ2=makeQuery(id+"F2.imprint","INTERSECT",VERTEX,{"derivedFrom":[subQ1,subQ0]});Q11=makeQuery(id+"F2.imprint","IMPRINT",FACE,{"disambiguationData":[TD([[makeQuery(id+"F2.imprint","IMPRINT",EDGE,{"disambiguationData":[TD([[subQ2,1.0]])],"derivedFrom":subQ1}),1.0]])]});}
            var Q12;
            {var subQ0=sQuery(id+"F2.wireOp",EDGE,"E32.5.0.3");var subQ1=sQuery(id+"F2.wireOp",EDGE,"E32.4.0.2");var subQ2=makeQuery(id+"F2.imprint","INTERSECT",VERTEX,{"derivedFrom":[subQ1,subQ0]});Q12=makeQuery(id+"F2.imprint","IMPRINT",FACE,{"disambiguationData":[TD([[makeQuery(id+"F2.imprint","IMPRINT",EDGE,{"disambiguationData":[TD([[subQ2,1.0]])],"derivedFrom":subQ1}),1.0]])]});}
            var Q13;
            {var subQ0=sQuery(id+"F2.wireOp",EDGE,"E32.17.0.3");var subQ1=sQuery(id+"F2.wireOp",EDGE,"E32.14.0.2");var subQ2=makeQuery(id+"F2.imprint","INTERSECT",VERTEX,{"derivedFrom":[subQ1,subQ0]});Q13=makeQuery(id+"F2.imprint","IMPRINT",FACE,{"disambiguationData":[TD([[makeQuery(id+"F2.imprint","IMPRINT",EDGE,{"disambiguationData":[TD([[subQ2,-1.0]])],"derivedFrom":subQ1}),1.0]])]});}
            var Q14;
            {var subQ0=sQuery(id+"F2.wireOp",EDGE,"E32.13.0.3");var subQ1=sQuery(id+"F2.wireOp",EDGE,"E32.10.0.2");var subQ2=makeQuery(id+"F2.imprint","INTERSECT",VERTEX,{"derivedFrom":[subQ1,subQ0]});Q14=makeQuery(id+"F2.imprint","IMPRINT",FACE,{"disambiguationData":[TD([[makeQuery(id+"F2.imprint","IMPRINT",EDGE,{"disambiguationData":[TD([[subQ2,-1.0]])],"derivedFrom":subQ1}),1.0]])]});}
            var Q15;
            {var subQ0=sQuery(id+"F2.wireOp",EDGE,"E32.14.0.2");var subQ1=sQuery(id+"F2.wireOp",EDGE,"E32.14.0.0");var subQ2=makeQuery(id+"F2.imprint","INTERSECT",VERTEX,{"derivedFrom":[subQ1,subQ0]});Q15=makeQuery(id+"F2.imprint","IMPRINT",FACE,{"disambiguationData":[TD([[makeQuery(id+"F2.imprint","IMPRINT",EDGE,{"disambiguationData":[TD([[subQ2,1.0]])],"derivedFrom":subQ1}),1.0]])]});}
            var Q16;
            {var subQ0=sQuery(id+"F2.wireOp",EDGE,"E32.14.0.3");var subQ1=sQuery(id+"F2.wireOp",EDGE,"E32.10.0.2");var subQ2=makeQuery(id+"F2.imprint","INTERSECT",VERTEX,{"derivedFrom":[subQ1,subQ0]});Q16=makeQuery(id+"F2.imprint","IMPRINT",FACE,{"disambiguationData":[TD([[makeQuery(id+"F2.imprint","IMPRINT",EDGE,{"disambiguationData":[TD([[subQ2,-1.0]])],"derivedFrom":subQ1}),1.0]])]});}
            var Q17;
            {var subQ0=sQuery(id+"F2.wireOp",EDGE,"E32.11.0.3");var subQ1=sQuery(id+"F2.wireOp",EDGE,"E32.7.0.2");var subQ2=makeQuery(id+"F2.imprint","INTERSECT",VERTEX,{"derivedFrom":[subQ1,subQ0]});Q17=makeQuery(id+"F2.imprint","IMPRINT",FACE,{"disambiguationData":[TD([[makeQuery(id+"F2.imprint","IMPRINT",EDGE,{"disambiguationData":[TD([[subQ2,-1.0]])],"derivedFrom":subQ1}),1.0]])]});}
            var Q18;
            {var subQ0=sQuery(id+"F2.wireOp",EDGE,"E32.7.0.3");var subQ1=sQuery(id+"F2.wireOp",EDGE,"E32.3.0.2");var subQ2=makeQuery(id+"F2.imprint","INTERSECT",VERTEX,{"derivedFrom":[subQ1,subQ0]});Q18=makeQuery(id+"F2.imprint","IMPRINT",FACE,{"disambiguationData":[TD([[makeQuery(id+"F2.imprint","IMPRINT",EDGE,{"disambiguationData":[TD([[subQ2,-1.0]])],"derivedFrom":subQ1}),1.0]])]});}
            var Q19;
            {var subQ0=sQuery(id+"F2.wireOp",EDGE,"E32.4.0.3");var subQ1=sQuery(id+"F2.wireOp",EDGE,"E31.2");var subQ2=makeQuery(id+"F2.imprint","INTERSECT",VERTEX,{"derivedFrom":[subQ1,subQ0]});Q19=makeQuery(id+"F2.imprint","IMPRINT",FACE,{"disambiguationData":[TD([[makeQuery(id+"F2.imprint","IMPRINT",EDGE,{"disambiguationData":[TD([[subQ2,-1.0]])],"derivedFrom":subQ1}),1.0]])]});}
            var Q20;
            {var subQ0=sQuery(id+"F2.wireOp",EDGE,"E32.15.0.3");var subQ1=sQuery(id+"F2.wireOp",EDGE,"E32.11.0.2");var subQ2=makeQuery(id+"F2.imprint","INTERSECT",VERTEX,{"derivedFrom":[subQ1,subQ0]});Q20=makeQuery(id+"F2.imprint","IMPRINT",FACE,{"disambiguationData":[TD([[makeQuery(id+"F2.imprint","IMPRINT",EDGE,{"disambiguationData":[TD([[subQ2,-1.0]])],"derivedFrom":subQ1}),1.0]])]});}
            var Q21;
            {var subQ0=sQuery(id+"F2.wireOp",EDGE,"E32.10.0.3");var subQ1=sQuery(id+"F2.wireOp",EDGE,"E32.9.0.2");var subQ2=makeQuery(id+"F2.imprint","INTERSECT",VERTEX,{"derivedFrom":[subQ1,subQ0]});Q21=makeQuery(id+"F2.imprint","IMPRINT",FACE,{"disambiguationData":[TD([[makeQuery(id+"F2.imprint","IMPRINT",EDGE,{"disambiguationData":[TD([[subQ2,1.0]])],"derivedFrom":subQ1}),1.0]])]});}
            var Q22;
            {var subQ0=sQuery(id+"F2.wireOp",EDGE,"E32.12.0.3");var subQ1=sQuery(id+"F2.wireOp",EDGE,"E32.8.0.2");var subQ2=makeQuery(id+"F2.imprint","INTERSECT",VERTEX,{"derivedFrom":[subQ1,subQ0]});Q22=makeQuery(id+"F2.imprint","IMPRINT",FACE,{"disambiguationData":[TD([[makeQuery(id+"F2.imprint","IMPRINT",EDGE,{"disambiguationData":[TD([[subQ2,-1.0]])],"derivedFrom":subQ1}),1.0]])]});}
            var Q23;
            {var subQ0=sQuery(id+"F2.wireOp",EDGE,"E32.8.0.3");var subQ1=sQuery(id+"F2.wireOp",EDGE,"E32.4.0.2");var subQ2=makeQuery(id+"F2.imprint","INTERSECT",VERTEX,{"derivedFrom":[subQ1,subQ0]});Q23=makeQuery(id+"F2.imprint","IMPRINT",FACE,{"disambiguationData":[TD([[makeQuery(id+"F2.imprint","IMPRINT",EDGE,{"disambiguationData":[TD([[subQ2,-1.0]])],"derivedFrom":subQ1}),1.0]])]});}
            var Q24;
            {var subQ0=sQuery(id+"F2.wireOp",EDGE,"E32.11.0.3");var subQ1=sQuery(id+"F2.wireOp",EDGE,"E32.8.0.2");var subQ2=makeQuery(id+"F2.imprint","INTERSECT",VERTEX,{"derivedFrom":[subQ1,subQ0]});Q24=makeQuery(id+"F2.imprint","IMPRINT",FACE,{"disambiguationData":[TD([[makeQuery(id+"F2.imprint","IMPRINT",EDGE,{"disambiguationData":[TD([[subQ2,-1.0]])],"derivedFrom":subQ1}),1.0]])]});}
            var Q25;
            {var subQ0=sQuery(id+"F2.wireOp",EDGE,"E32.7.0.3");var subQ1=sQuery(id+"F2.wireOp",EDGE,"E32.4.0.2");var subQ2=makeQuery(id+"F2.imprint","INTERSECT",VERTEX,{"derivedFrom":[subQ1,subQ0]});Q25=makeQuery(id+"F2.imprint","IMPRINT",FACE,{"disambiguationData":[TD([[makeQuery(id+"F2.imprint","IMPRINT",EDGE,{"disambiguationData":[TD([[subQ2,-1.0]])],"derivedFrom":subQ1}),1.0]])]});}
            var Q26;
            {var subQ0=sQuery(id+"F2.wireOp",EDGE,"E32.3.0.3");var subQ1=sQuery(id+"F2.wireOp",EDGE,"E31.2");var subQ2=makeQuery(id+"F2.imprint","INTERSECT",VERTEX,{"derivedFrom":[subQ1,subQ0]});Q26=makeQuery(id+"F2.imprint","IMPRINT",FACE,{"disambiguationData":[TD([[makeQuery(id+"F2.imprint","IMPRINT",EDGE,{"disambiguationData":[TD([[subQ2,-1.0]])],"derivedFrom":subQ1}),1.0]])]});}
            var Q27;
            {var subQ0=sQuery(id+"F2.wireOp",EDGE,"E32.15.0.3");var subQ1=sQuery(id+"F2.wireOp",EDGE,"E32.12.0.2");var subQ2=makeQuery(id+"F2.imprint","INTERSECT",VERTEX,{"derivedFrom":[subQ1,subQ0]});Q27=makeQuery(id+"F2.imprint","IMPRINT",FACE,{"disambiguationData":[TD([[makeQuery(id+"F2.imprint","IMPRINT",EDGE,{"disambiguationData":[TD([[subQ2,-1.0]])],"derivedFrom":subQ1}),1.0]])]});}
            var Q28;
            {var subQ0=sQuery(id+"F2.wireOp",EDGE,"E32.12.0.3");var subQ1=sQuery(id+"F2.wireOp",EDGE,"E32.11.0.2");var subQ2=makeQuery(id+"F2.imprint","INTERSECT",VERTEX,{"derivedFrom":[subQ1,subQ0]});Q28=makeQuery(id+"F2.imprint","IMPRINT",FACE,{"disambiguationData":[TD([[makeQuery(id+"F2.imprint","IMPRINT",EDGE,{"disambiguationData":[TD([[subQ2,1.0]])],"derivedFrom":subQ1}),1.0]])]});}
            var Q29;
            {var subQ5=sQuery(id+"F2.wireOp",EDGE,"E32.9.0.2");var subQ6=sQuery(id+"F2.wireOp",EDGE,"E32.9.0.0");var subQ7=makeQuery(id+"F2.imprint","INTERSECT",VERTEX,{"derivedFrom":[subQ6,subQ5]});Q29=makeQuery(id+"F2.imprint","IMPRINT",FACE,{"disambiguationData":[TD([[makeQuery(id+"F2.imprint","IMPRINT",EDGE,{"disambiguationData":[TD([[subQ7,1.0]])],"derivedFrom":subQ6}),1.0]])]});}
            var Q30;
            {var subQ0=sQuery(id+"F2.wireOp",EDGE,"E32.13.0.3");var subQ1=sQuery(id+"F2.wireOp",EDGE,"E32.9.0.2");var subQ2=makeQuery(id+"F2.imprint","INTERSECT",VERTEX,{"derivedFrom":[subQ1,subQ0]});Q30=makeQuery(id+"F2.imprint","IMPRINT",FACE,{"disambiguationData":[TD([[makeQuery(id+"F2.imprint","IMPRINT",EDGE,{"disambiguationData":[TD([[subQ2,-1.0]])],"derivedFrom":subQ1}),1.0]])]});}
            var Q31;
            {var subQ0=sQuery(id+"F2.wireOp",EDGE,"E32.9.0.3");var subQ1=sQuery(id+"F2.wireOp",EDGE,"E32.5.0.2");var subQ2=makeQuery(id+"F2.imprint","INTERSECT",VERTEX,{"derivedFrom":[subQ1,subQ0]});Q31=makeQuery(id+"F2.imprint","IMPRINT",FACE,{"disambiguationData":[TD([[makeQuery(id+"F2.imprint","IMPRINT",EDGE,{"disambiguationData":[TD([[subQ2,-1.0]])],"derivedFrom":subQ1}),1.0]])]});}
            var Q32;
            {var subQ0=sQuery(id+"F2.wireOp",EDGE,"E32.5.0.3");var subQ1=sQuery(id+"F2.wireOp",EDGE,"E32.1.0.2");var subQ2=makeQuery(id+"F2.imprint","INTERSECT",VERTEX,{"derivedFrom":[subQ1,subQ0]});Q32=makeQuery(id+"F2.imprint","IMPRINT",FACE,{"disambiguationData":[TD([[makeQuery(id+"F2.imprint","IMPRINT",EDGE,{"disambiguationData":[TD([[subQ2,-1.0]])],"derivedFrom":subQ1}),1.0]])]});}
            var Q33;
            {var subQ0=sQuery(id+"F2.wireOp",EDGE,"E32.12.0.3");var subQ1=sQuery(id+"F2.wireOp",EDGE,"E32.9.0.2");var subQ2=makeQuery(id+"F2.imprint","INTERSECT",VERTEX,{"derivedFrom":[subQ1,subQ0]});Q33=makeQuery(id+"F2.imprint","IMPRINT",FACE,{"disambiguationData":[TD([[makeQuery(id+"F2.imprint","IMPRINT",EDGE,{"disambiguationData":[TD([[subQ2,-1.0]])],"derivedFrom":subQ1}),1.0]])]});}
            var Q34;
            {var subQ0=sQuery(id+"F2.wireOp",EDGE,"E32.8.0.3");var subQ1=sQuery(id+"F2.wireOp",EDGE,"E32.5.0.2");var subQ2=makeQuery(id+"F2.imprint","INTERSECT",VERTEX,{"derivedFrom":[subQ1,subQ0]});Q34=makeQuery(id+"F2.imprint","IMPRINT",FACE,{"disambiguationData":[TD([[makeQuery(id+"F2.imprint","IMPRINT",EDGE,{"disambiguationData":[TD([[subQ2,-1.0]])],"derivedFrom":subQ1}),1.0]])]});}
            var Q35;
            {var subQ0=sQuery(id+"F2.wireOp",EDGE,"E32.4.0.3");var subQ1=sQuery(id+"F2.wireOp",EDGE,"E32.1.0.2");var subQ2=makeQuery(id+"F2.imprint","INTERSECT",VERTEX,{"derivedFrom":[subQ1,subQ0]});Q35=makeQuery(id+"F2.imprint","IMPRINT",FACE,{"disambiguationData":[TD([[makeQuery(id+"F2.imprint","IMPRINT",EDGE,{"disambiguationData":[TD([[subQ2,-1.0]])],"derivedFrom":subQ1}),1.0]])]});}
            var Q36;
            {var subQ0=sQuery(id+"F2.wireOp",EDGE,"E32.8.0.3");var subQ1=sQuery(id+"F2.wireOp",EDGE,"E32.7.0.2");var subQ2=makeQuery(id+"F2.imprint","INTERSECT",VERTEX,{"derivedFrom":[subQ1,subQ0]});Q36=makeQuery(id+"F2.imprint","IMPRINT",FACE,{"disambiguationData":[TD([[makeQuery(id+"F2.imprint","IMPRINT",EDGE,{"disambiguationData":[TD([[subQ2,1.0]])],"derivedFrom":subQ1}),1.0]])]});}
            var Q37;
            {var subQ0=sQuery(id+"F2.wireOp",EDGE,"E32.16.0.3");var subQ1=sQuery(id+"F2.wireOp",EDGE,"E32.13.0.2");var subQ2=makeQuery(id+"F2.imprint","INTERSECT",VERTEX,{"derivedFrom":[subQ1,subQ0]});Q37=makeQuery(id+"F2.imprint","IMPRINT",FACE,{"disambiguationData":[TD([[makeQuery(id+"F2.imprint","IMPRINT",EDGE,{"disambiguationData":[TD([[subQ2,-1.0]])],"derivedFrom":subQ1}),1.0]])]});}
            var Q38;
            {var subQ0=sQuery(id+"F2.wireOp",EDGE,"E32.5.0.3");var subQ1=sQuery(id+"F2.wireOp",EDGE,"E32.2.0.2");var subQ2=makeQuery(id+"F2.imprint","INTERSECT",VERTEX,{"derivedFrom":[subQ1,subQ0]});Q38=makeQuery(id+"F2.imprint","IMPRINT",FACE,{"disambiguationData":[TD([[makeQuery(id+"F2.imprint","IMPRINT",EDGE,{"disambiguationData":[TD([[subQ2,-1.0]])],"derivedFrom":subQ1}),1.0]])]});}
            var Q39;
            {var subQ0=sQuery(id+"F2.wireOp",EDGE,"E32.9.0.3");var subQ1=sQuery(id+"F2.wireOp",EDGE,"E32.6.0.2");var subQ2=makeQuery(id+"F2.imprint","INTERSECT",VERTEX,{"derivedFrom":[subQ1,subQ0]});Q39=makeQuery(id+"F2.imprint","IMPRINT",FACE,{"disambiguationData":[TD([[makeQuery(id+"F2.imprint","IMPRINT",EDGE,{"disambiguationData":[TD([[subQ2,-1.0]])],"derivedFrom":subQ1}),1.0]])]});}
            var Q40;
            {var subQ0=sQuery(id+"F2.wireOp",EDGE,"E31.0");Q40=makeQuery(id+"F2.imprint","IMPRINT",FACE,{"disambiguationData":[TD([[makeQuery(id+"F2.imprint","IMPRINT",EDGE,{"derivedFrom":subQ0}),-1.0]])]});}
            var Q41;
            {var subQ0=sQuery(id+"F2.wireOp",EDGE,"E32.9.0.3");var subQ1=sQuery(id+"F2.wireOp",EDGE,"E32.8.0.2");var subQ2=makeQuery(id+"F2.imprint","INTERSECT",VERTEX,{"derivedFrom":[subQ1,subQ0]});Q41=makeQuery(id+"F2.imprint","IMPRINT",FACE,{"disambiguationData":[TD([[makeQuery(id+"F2.imprint","IMPRINT",EDGE,{"disambiguationData":[TD([[subQ2,1.0]])],"derivedFrom":subQ1}),1.0]])]});}
            var Q42;
            {var subQ0=sQuery(id+"F2.wireOp",EDGE,"E32.3.0.3");var subQ1=sQuery(id+"F2.wireOp",EDGE,"E31.1");var subQ2=makeQuery(id+"F2.imprint","INTERSECT",VERTEX,{"derivedFrom":[subQ1,subQ0]});Q42=makeQuery(id+"F2.imprint","IMPRINT",FACE,{"disambiguationData":[TD([[makeQuery(id+"F2.imprint","IMPRINT",EDGE,{"disambiguationData":[TD([[subQ2,-1.0]])],"derivedFrom":subQ1}),-1.0]])]});}
            var Q43;
            {var subQ0=sQuery(id+"F2.wireOp",EDGE,"E32.6.0.3");var subQ1=sQuery(id+"F2.wireOp",EDGE,"E32.2.0.2");var subQ2=makeQuery(id+"F2.imprint","INTERSECT",VERTEX,{"derivedFrom":[subQ1,subQ0]});Q43=makeQuery(id+"F2.imprint","IMPRINT",FACE,{"disambiguationData":[TD([[makeQuery(id+"F2.imprint","IMPRINT",EDGE,{"disambiguationData":[TD([[subQ2,-1.0]])],"derivedFrom":subQ1}),1.0]])]});}
            var Q44;
            {var subQ0=sQuery(id+"F2.wireOp",EDGE,"E32.10.0.3");var subQ1=sQuery(id+"F2.wireOp",EDGE,"E32.6.0.2");var subQ2=makeQuery(id+"F2.imprint","INTERSECT",VERTEX,{"derivedFrom":[subQ1,subQ0]});Q44=makeQuery(id+"F2.imprint","IMPRINT",FACE,{"disambiguationData":[TD([[makeQuery(id+"F2.imprint","IMPRINT",EDGE,{"disambiguationData":[TD([[subQ2,-1.0]])],"derivedFrom":subQ1}),1.0]])]});}
            var Q45;
            {var subQ0=sQuery(id+"F2.wireOp",EDGE,"E32.1.0.3");var subQ1=sQuery(id+"F2.wireOp",EDGE,"E31.2");var subQ2=makeQuery(id+"F2.imprint","INTERSECT",VERTEX,{"derivedFrom":[subQ1,subQ0]});Q45=makeQuery(id+"F2.imprint","IMPRINT",FACE,{"disambiguationData":[TD([[makeQuery(id+"F2.imprint","IMPRINT",EDGE,{"disambiguationData":[TD([[subQ2,1.0]])],"derivedFrom":subQ1}),1.0]])]});}
            var Q46;
            {var subQ0=sQuery(id+"F2.wireOp",EDGE,"E32.6.0.3");var subQ1=sQuery(id+"F2.wireOp",EDGE,"E32.3.0.2");var subQ2=makeQuery(id+"F2.imprint","INTERSECT",VERTEX,{"derivedFrom":[subQ1,subQ0]});Q46=makeQuery(id+"F2.imprint","IMPRINT",FACE,{"disambiguationData":[TD([[makeQuery(id+"F2.imprint","IMPRINT",EDGE,{"disambiguationData":[TD([[subQ2,-1.0]])],"derivedFrom":subQ1}),1.0]])]});}
            var Q47;
            {var subQ0=sQuery(id+"F2.wireOp",EDGE,"E32.2.0.3");var subQ1=sQuery(id+"F2.wireOp",EDGE,"E32.1.0.2");var subQ2=makeQuery(id+"F2.imprint","INTERSECT",VERTEX,{"derivedFrom":[subQ1,subQ0]});Q47=makeQuery(id+"F2.imprint","IMPRINT",FACE,{"disambiguationData":[TD([[makeQuery(id+"F2.imprint","IMPRINT",EDGE,{"disambiguationData":[TD([[subQ2,1.0]])],"derivedFrom":subQ1}),1.0]])]});}
            var Q48;
            {var subQ0=sQuery(id+"F2.wireOp",EDGE,"E32.11.0.3");var subQ1=sQuery(id+"F2.wireOp",EDGE,"E32.10.0.2");var subQ2=makeQuery(id+"F2.imprint","INTERSECT",VERTEX,{"derivedFrom":[subQ1,subQ0]});Q48=makeQuery(id+"F2.imprint","IMPRINT",FACE,{"disambiguationData":[TD([[makeQuery(id+"F2.imprint","IMPRINT",EDGE,{"disambiguationData":[TD([[subQ2,1.0]])],"derivedFrom":subQ1}),1.0]])]});}
            var Q49;
            {var subQ0=sQuery(id+"F2.wireOp",EDGE,"E32.10.0.3");var subQ1=sQuery(id+"F2.wireOp",EDGE,"E32.7.0.2");var subQ2=makeQuery(id+"F2.imprint","INTERSECT",VERTEX,{"derivedFrom":[subQ1,subQ0]});Q49=makeQuery(id+"F2.imprint","IMPRINT",FACE,{"disambiguationData":[TD([[makeQuery(id+"F2.imprint","IMPRINT",EDGE,{"disambiguationData":[TD([[subQ2,-1.0]])],"derivedFrom":subQ1}),1.0]])]});}
            var Q50;
            {var subQ0=sQuery(id+"F2.wireOp",EDGE,"E32.14.0.3");var subQ1=sQuery(id+"F2.wireOp",EDGE,"E32.11.0.2");var subQ2=makeQuery(id+"F2.imprint","INTERSECT",VERTEX,{"derivedFrom":[subQ1,subQ0]});Q50=makeQuery(id+"F2.imprint","IMPRINT",FACE,{"disambiguationData":[TD([[makeQuery(id+"F2.imprint","IMPRINT",EDGE,{"disambiguationData":[TD([[subQ2,-1.0]])],"derivedFrom":subQ1}),1.0]])]});}
            var Q51;
            {var subQ8=sQuery(id+"F2.wireOp",EDGE,"E32.1.0.2");var subQ9=sQuery(id+"F2.wireOp",EDGE,"E32.1.0.0");var subQ10=makeQuery(id+"F2.imprint","INTERSECT",VERTEX,{"derivedFrom":[subQ9,subQ8]});Q51=makeQuery(id+"F2.imprint","IMPRINT",FACE,{"disambiguationData":[TD([[makeQuery(id+"F2.imprint","IMPRINT",EDGE,{"disambiguationData":[TD([[subQ10,1.0]])],"derivedFrom":subQ9}),1.0]])]});}
            var Q52;
            {var subQ5=sQuery(id+"F2.wireOp",EDGE,"E31.1");var subQ10=sQuery(id+"F2.wireOp",EDGE,"E31.2");var subQ11=makeQuery(id+"F2.imprint","INTERSECT",VERTEX,{"derivedFrom":[subQ5,subQ10]});Q52=makeQuery(id+"F2.imprint","IMPRINT",FACE,{"disambiguationData":[TD([[makeQuery(id+"F2.imprint","IMPRINT",EDGE,{"disambiguationData":[TD([[subQ11,1.0]])],"derivedFrom":subQ5}),1.0]])]});}
            var Q53;
            {var subQ0=sQuery(id+"F2.wireOp",EDGE,"E32.16.0.3");var subQ1=sQuery(id+"F2.wireOp",EDGE,"E32.12.0.2");var subQ2=makeQuery(id+"F2.imprint","INTERSECT",VERTEX,{"derivedFrom":[subQ1,subQ0]});Q53=makeQuery(id+"F2.imprint","IMPRINT",FACE,{"disambiguationData":[TD([[makeQuery(id+"F2.imprint","IMPRINT",EDGE,{"disambiguationData":[TD([[subQ2,-1.0]])],"derivedFrom":subQ1}),1.0]])]});}
            var Q54;
            {var subQ8=sQuery(id+"F2.wireOp",EDGE,"E32.5.0.2");var subQ9=sQuery(id+"F2.wireOp",EDGE,"E32.5.0.0");var subQ10=makeQuery(id+"F2.imprint","INTERSECT",VERTEX,{"derivedFrom":[subQ9,subQ8]});Q54=makeQuery(id+"F2.imprint","IMPRINT",FACE,{"disambiguationData":[TD([[makeQuery(id+"F2.imprint","IMPRINT",EDGE,{"disambiguationData":[TD([[subQ10,1.0]])],"derivedFrom":subQ9}),1.0]])]});}
            var Q55;
            {var subQ0=sQuery(id+"F2.wireOp",EDGE,"E32.2.0.2");var subQ1=sQuery(id+"F2.wireOp",EDGE,"E32.2.0.0");var subQ2=makeQuery(id+"F2.imprint","INTERSECT",VERTEX,{"derivedFrom":[subQ1,subQ0]});Q55=makeQuery(id+"F2.imprint","IMPRINT",FACE,{"disambiguationData":[TD([[makeQuery(id+"F2.imprint","IMPRINT",EDGE,{"disambiguationData":[TD([[subQ2,1.0]])],"derivedFrom":subQ1}),1.0]])]});}
            var Q56;
            {var subQ8=sQuery(id+"F2.wireOp",EDGE,"E32.6.0.2");var subQ9=sQuery(id+"F2.wireOp",EDGE,"E32.6.0.0");var subQ10=makeQuery(id+"F2.imprint","INTERSECT",VERTEX,{"derivedFrom":[subQ9,subQ8]});Q56=makeQuery(id+"F2.imprint","IMPRINT",FACE,{"disambiguationData":[TD([[makeQuery(id+"F2.imprint","IMPRINT",EDGE,{"disambiguationData":[TD([[subQ10,1.0]])],"derivedFrom":subQ9}),1.0]])]});}
            var Q57;
            {var subQ8=sQuery(id+"F2.wireOp",EDGE,"E32.7.0.2");var subQ9=sQuery(id+"F2.wireOp",EDGE,"E32.7.0.0");var subQ10=makeQuery(id+"F2.imprint","INTERSECT",VERTEX,{"derivedFrom":[subQ9,subQ8]});Q57=makeQuery(id+"F2.imprint","IMPRINT",FACE,{"disambiguationData":[TD([[makeQuery(id+"F2.imprint","IMPRINT",EDGE,{"disambiguationData":[TD([[subQ10,1.0]])],"derivedFrom":subQ9}),1.0]])]});}
            var Q58;
            {var subQ5=sQuery(id+"F2.wireOp",EDGE,"E32.8.0.2");var subQ6=sQuery(id+"F2.wireOp",EDGE,"E32.8.0.0");var subQ7=makeQuery(id+"F2.imprint","INTERSECT",VERTEX,{"derivedFrom":[subQ6,subQ5]});Q58=makeQuery(id+"F2.imprint","IMPRINT",FACE,{"disambiguationData":[TD([[makeQuery(id+"F2.imprint","IMPRINT",EDGE,{"disambiguationData":[TD([[subQ7,1.0]])],"derivedFrom":subQ6}),1.0]])]});}
            var Q59;
            {var subQ6=sQuery(id+"F2.wireOp",EDGE,"E32.13.0.2");var subQ7=sQuery(id+"F2.wireOp",EDGE,"E32.13.0.0");var subQ8=makeQuery(id+"F2.imprint","INTERSECT",VERTEX,{"derivedFrom":[subQ7,subQ6]});Q59=makeQuery(id+"F2.imprint","IMPRINT",FACE,{"disambiguationData":[TD([[makeQuery(id+"F2.imprint","IMPRINT",EDGE,{"disambiguationData":[TD([[subQ8,1.0]])],"derivedFrom":subQ7}),1.0]])]});}
            var Q60;
            {var subQ0=sQuery(id+"F2.wireOp",EDGE,"E32.17.0.3");var subQ1=sQuery(id+"F2.wireOp",EDGE,"E32.13.0.2");var subQ2=makeQuery(id+"F2.imprint","INTERSECT",VERTEX,{"derivedFrom":[subQ1,subQ0]});Q60=makeQuery(id+"F2.imprint","IMPRINT",FACE,{"disambiguationData":[TD([[makeQuery(id+"F2.imprint","IMPRINT",EDGE,{"disambiguationData":[TD([[subQ2,-1.0]])],"derivedFrom":subQ1}),1.0]])]});}
            var Q61;
            {var subQ8=sQuery(id+"F2.wireOp",EDGE,"E32.10.0.0");var subQ10=sQuery(id+"F2.wireOp",EDGE,"E32.10.0.2");var subQ11=makeQuery(id+"F2.imprint","INTERSECT",VERTEX,{"derivedFrom":[subQ8,subQ10]});Q61=makeQuery(id+"F2.imprint","IMPRINT",FACE,{"disambiguationData":[TD([[makeQuery(id+"F2.imprint","IMPRINT",EDGE,{"disambiguationData":[TD([[subQ11,1.0]])],"derivedFrom":subQ8}),1.0]])]});}
            var Q62;
            {var subQ8=sQuery(id+"F2.wireOp",EDGE,"E32.11.0.2");var subQ9=sQuery(id+"F2.wireOp",EDGE,"E32.11.0.0");var subQ10=makeQuery(id+"F2.imprint","INTERSECT",VERTEX,{"derivedFrom":[subQ9,subQ8]});Q62=makeQuery(id+"F2.imprint","IMPRINT",FACE,{"disambiguationData":[TD([[makeQuery(id+"F2.imprint","IMPRINT",EDGE,{"disambiguationData":[TD([[subQ10,1.0]])],"derivedFrom":subQ9}),1.0]])]});}
            var Q63;
            {var subQ8=sQuery(id+"F2.wireOp",EDGE,"E32.12.0.2");var subQ9=sQuery(id+"F2.wireOp",EDGE,"E32.12.0.0");var subQ10=makeQuery(id+"F2.imprint","INTERSECT",VERTEX,{"derivedFrom":[subQ9,subQ8]});Q63=makeQuery(id+"F2.imprint","IMPRINT",FACE,{"disambiguationData":[TD([[makeQuery(id+"F2.imprint","IMPRINT",EDGE,{"disambiguationData":[TD([[subQ10,1.0]])],"derivedFrom":subQ9}),1.0]])]});}
            var Q64;
            {var subQ8=sQuery(id+"F2.wireOp",EDGE,"E32.3.0.2");var subQ9=sQuery(id+"F2.wireOp",EDGE,"E32.3.0.0");var subQ10=makeQuery(id+"F2.imprint","INTERSECT",VERTEX,{"derivedFrom":[subQ9,subQ8]});Q64=makeQuery(id+"F2.imprint","IMPRINT",FACE,{"disambiguationData":[TD([[makeQuery(id+"F2.imprint","IMPRINT",EDGE,{"disambiguationData":[TD([[subQ10,1.0]])],"derivedFrom":subQ9}),1.0]])]});}
            var Q65;
            {var subQ5=sQuery(id+"F2.wireOp",EDGE,"E32.4.0.2");var subQ6=sQuery(id+"F2.wireOp",EDGE,"E32.4.0.0");var subQ7=makeQuery(id+"F2.imprint","INTERSECT",VERTEX,{"derivedFrom":[subQ6,subQ5]});Q65=makeQuery(id+"F2.imprint","IMPRINT",FACE,{"disambiguationData":[TD([[makeQuery(id+"F2.imprint","IMPRINT",EDGE,{"disambiguationData":[TD([[subQ7,1.0]])],"derivedFrom":subQ6}),1.0]])]});}
            var Q66;
            {var subQ0=sQuery(id+"F2.wireOp",EDGE,"E32.9.0.3");var subQ1=sQuery(id+"F2.wireOp",EDGE,"E32.7.0.0");var subQ2=makeQuery(id+"F2.imprint","INTERSECT",VERTEX,{"derivedFrom":[subQ1,subQ0]});Q66=makeQuery(id+"F2.imprint","IMPRINT",FACE,{"disambiguationData":[TD([[makeQuery(id+"F2.imprint","IMPRINT",EDGE,{"disambiguationData":[TD([[subQ2,-1.0]])],"derivedFrom":subQ1}),1.0]])]});}
            var Q67;
            {var subQ0=sQuery(id+"F2.wireOp",EDGE,"E32.11.0.3");var subQ1=sQuery(id+"F2.wireOp",EDGE,"E32.10.0.0");var subQ2=makeQuery(id+"F2.imprint","INTERSECT",VERTEX,{"derivedFrom":[subQ1,subQ0]});Q67=makeQuery(id+"F2.imprint","IMPRINT",FACE,{"disambiguationData":[TD([[makeQuery(id+"F2.imprint","IMPRINT",EDGE,{"disambiguationData":[TD([[subQ2,-1.0]])],"derivedFrom":subQ1}),1.0]])]});}
            var Q68;
            {var subQ0=sQuery(id+"F2.wireOp",EDGE,"E32.13.0.3");var subQ1=sQuery(id+"F2.wireOp",EDGE,"E32.11.0.0");var subQ2=makeQuery(id+"F2.imprint","INTERSECT",VERTEX,{"derivedFrom":[subQ1,subQ0]});Q68=makeQuery(id+"F2.imprint","IMPRINT",FACE,{"disambiguationData":[TD([[makeQuery(id+"F2.imprint","IMPRINT",EDGE,{"disambiguationData":[TD([[subQ2,-1.0]])],"derivedFrom":subQ1}),1.0]])]});}
            var Q69;
            {var subQ0=sQuery(id+"F2.wireOp",EDGE,"E32.6.0.3");var subQ1=sQuery(id+"F2.wireOp",EDGE,"E32.3.0.0");var subQ2=makeQuery(id+"F2.imprint","INTERSECT",VERTEX,{"derivedFrom":[subQ1,subQ0]});Q69=makeQuery(id+"F2.imprint","IMPRINT",FACE,{"disambiguationData":[TD([[makeQuery(id+"F2.imprint","IMPRINT",EDGE,{"disambiguationData":[TD([[subQ2,-1.0]])],"derivedFrom":subQ1}),1.0]])]});}
            var Q70;
            {var subQ0=sQuery(id+"F2.wireOp",EDGE,"E32.14.0.3");var subQ1=sQuery(id+"F2.wireOp",EDGE,"E32.11.0.0");var subQ2=makeQuery(id+"F2.imprint","INTERSECT",VERTEX,{"derivedFrom":[subQ1,subQ0]});Q70=makeQuery(id+"F2.imprint","IMPRINT",FACE,{"disambiguationData":[TD([[makeQuery(id+"F2.imprint","IMPRINT",EDGE,{"disambiguationData":[TD([[subQ2,-1.0]])],"derivedFrom":subQ1}),1.0]])]});}
            var Q71;
            {var subQ0=sQuery(id+"F2.wireOp",EDGE,"E32.16.0.3");var subQ1=sQuery(id+"F2.wireOp",EDGE,"E32.15.0.0");var subQ2=makeQuery(id+"F2.imprint","INTERSECT",VERTEX,{"derivedFrom":[subQ1,subQ0]});Q71=makeQuery(id+"F2.imprint","IMPRINT",FACE,{"disambiguationData":[TD([[makeQuery(id+"F2.imprint","IMPRINT",EDGE,{"disambiguationData":[TD([[subQ2,-1.0]])],"derivedFrom":subQ1}),1.0]])]});}
            var Q72;
            {var subQ0=sQuery(id+"F2.wireOp",EDGE,"E32.14.0.3");var subQ1=sQuery(id+"F2.wireOp",EDGE,"E32.12.0.0");var subQ2=makeQuery(id+"F2.imprint","INTERSECT",VERTEX,{"derivedFrom":[subQ1,subQ0]});Q72=makeQuery(id+"F2.imprint","IMPRINT",FACE,{"disambiguationData":[TD([[makeQuery(id+"F2.imprint","IMPRINT",EDGE,{"disambiguationData":[TD([[subQ2,-1.0]])],"derivedFrom":subQ1}),1.0]])]});}
            var Q73;
            {var subQ0=sQuery(id+"F2.wireOp",EDGE,"E32.12.0.3");var subQ1=sQuery(id+"F2.wireOp",EDGE,"E32.11.0.0");var subQ2=makeQuery(id+"F2.imprint","INTERSECT",VERTEX,{"derivedFrom":[subQ1,subQ0]});Q73=makeQuery(id+"F2.imprint","IMPRINT",FACE,{"disambiguationData":[TD([[makeQuery(id+"F2.imprint","IMPRINT",EDGE,{"disambiguationData":[TD([[subQ2,-1.0]])],"derivedFrom":subQ1}),1.0]])]});}
            var Q74;
            {var subQ0=sQuery(id+"F2.wireOp",EDGE,"E32.8.0.2");var subQ1=sQuery(id+"F2.wireOp",EDGE,"E32.8.0.0");var subQ2=makeQuery(id+"F2.imprint","INTERSECT",VERTEX,{"derivedFrom":[subQ1,subQ0]});Q74=makeQuery(id+"F2.imprint","IMPRINT",FACE,{"disambiguationData":[TD([[makeQuery(id+"F2.imprint","IMPRINT",EDGE,{"disambiguationData":[TD([[subQ2,1.0]])],"derivedFrom":subQ1}),-1.0]])]});}
            var Q75;
            {var subQ0=sQuery(id+"F2.wireOp",EDGE,"E32.4.0.2");var subQ1=sQuery(id+"F2.wireOp",EDGE,"E32.4.0.0");var subQ2=makeQuery(id+"F2.imprint","INTERSECT",VERTEX,{"derivedFrom":[subQ1,subQ0]});Q75=makeQuery(id+"F2.imprint","IMPRINT",FACE,{"disambiguationData":[TD([[makeQuery(id+"F2.imprint","IMPRINT",EDGE,{"disambiguationData":[TD([[subQ2,1.0]])],"derivedFrom":subQ1}),-1.0]])]});}
            var Q76;
            {var subQ0=sQuery(id+"F2.wireOp",EDGE,"E32.7.0.3");var subQ1=sQuery(id+"F2.wireOp",EDGE,"E32.4.0.0");var subQ2=makeQuery(id+"F2.imprint","INTERSECT",VERTEX,{"derivedFrom":[subQ1,subQ0]});Q76=makeQuery(id+"F2.imprint","IMPRINT",FACE,{"disambiguationData":[TD([[makeQuery(id+"F2.imprint","IMPRINT",EDGE,{"disambiguationData":[TD([[subQ2,-1.0]])],"derivedFrom":subQ1}),1.0]])]});}
            var Q77;
            {var subQ0=sQuery(id+"F2.wireOp",EDGE,"E32.15.0.3");var subQ1=sQuery(id+"F2.wireOp",EDGE,"E32.12.0.0");var subQ2=makeQuery(id+"F2.imprint","INTERSECT",VERTEX,{"derivedFrom":[subQ1,subQ0]});Q77=makeQuery(id+"F2.imprint","IMPRINT",FACE,{"disambiguationData":[TD([[makeQuery(id+"F2.imprint","IMPRINT",EDGE,{"disambiguationData":[TD([[subQ2,-1.0]])],"derivedFrom":subQ1}),1.0]])]});}
            var Q78;
            {var subQ0=sQuery(id+"F2.wireOp",EDGE,"E32.7.0.3");var subQ1=sQuery(id+"F2.wireOp",EDGE,"E32.6.0.0");var subQ2=makeQuery(id+"F2.imprint","INTERSECT",VERTEX,{"derivedFrom":[subQ1,subQ0]});Q78=makeQuery(id+"F2.imprint","IMPRINT",FACE,{"disambiguationData":[TD([[makeQuery(id+"F2.imprint","IMPRINT",EDGE,{"disambiguationData":[TD([[subQ2,-1.0]])],"derivedFrom":subQ1}),1.0]])]});}
            var Q79;
            {var subQ0=sQuery(id+"F2.wireOp",EDGE,"E32.6.0.2");var subQ1=sQuery(id+"F2.wireOp",EDGE,"E32.6.0.0");var subQ2=makeQuery(id+"F2.imprint","INTERSECT",VERTEX,{"derivedFrom":[subQ1,subQ0]});Q79=makeQuery(id+"F2.imprint","IMPRINT",FACE,{"disambiguationData":[TD([[makeQuery(id+"F2.imprint","IMPRINT",EDGE,{"disambiguationData":[TD([[subQ2,1.0]])],"derivedFrom":subQ1}),-1.0]])]});}
            var Q80;
            {var subQ0=sQuery(id+"F2.wireOp",EDGE,"E32.16.0.3");var subQ1=sQuery(id+"F2.wireOp",EDGE,"E32.13.0.0");var subQ2=makeQuery(id+"F2.imprint","INTERSECT",VERTEX,{"derivedFrom":[subQ1,subQ0]});Q80=makeQuery(id+"F2.imprint","IMPRINT",FACE,{"disambiguationData":[TD([[makeQuery(id+"F2.imprint","IMPRINT",EDGE,{"disambiguationData":[TD([[subQ2,-1.0]])],"derivedFrom":subQ1}),1.0]])]});}
            var Q81;
            {var subQ0=sQuery(id+"F2.wireOp",EDGE,"E32.8.0.3");var subQ1=sQuery(id+"F2.wireOp",EDGE,"E32.5.0.0");var subQ2=makeQuery(id+"F2.imprint","INTERSECT",VERTEX,{"derivedFrom":[subQ1,subQ0]});Q81=makeQuery(id+"F2.imprint","IMPRINT",FACE,{"disambiguationData":[TD([[makeQuery(id+"F2.imprint","IMPRINT",EDGE,{"disambiguationData":[TD([[subQ2,-1.0]])],"derivedFrom":subQ1}),1.0]])]});}
            var Q82;
            {var subQ0=sQuery(id+"F2.wireOp",EDGE,"E32.4.0.3");var subQ1=sQuery(id+"F2.wireOp",EDGE,"E32.1.0.0");var subQ2=makeQuery(id+"F2.imprint","INTERSECT",VERTEX,{"derivedFrom":[subQ1,subQ0]});Q82=makeQuery(id+"F2.imprint","IMPRINT",FACE,{"disambiguationData":[TD([[makeQuery(id+"F2.imprint","IMPRINT",EDGE,{"disambiguationData":[TD([[subQ2,-1.0]])],"derivedFrom":subQ1}),1.0]])]});}
            var Q83;
            {var subQ0=sQuery(id+"F2.wireOp",EDGE,"E32.8.0.3");var subQ1=sQuery(id+"F2.wireOp",EDGE,"E32.7.0.0");var subQ2=makeQuery(id+"F2.imprint","INTERSECT",VERTEX,{"derivedFrom":[subQ1,subQ0]});Q83=makeQuery(id+"F2.imprint","IMPRINT",FACE,{"disambiguationData":[TD([[makeQuery(id+"F2.imprint","IMPRINT",EDGE,{"disambiguationData":[TD([[subQ2,-1.0]])],"derivedFrom":subQ1}),1.0]])]});}
            var Q84;
            {var subQ0=sQuery(id+"F2.wireOp",EDGE,"E32.7.0.2");var subQ1=sQuery(id+"F2.wireOp",EDGE,"E32.7.0.0");var subQ2=makeQuery(id+"F2.imprint","INTERSECT",VERTEX,{"derivedFrom":[subQ1,subQ0]});Q84=makeQuery(id+"F2.imprint","IMPRINT",FACE,{"disambiguationData":[TD([[makeQuery(id+"F2.imprint","IMPRINT",EDGE,{"disambiguationData":[TD([[subQ2,1.0]])],"derivedFrom":subQ1}),-1.0]])]});}
            var Q85;
            {var subQ0=sQuery(id+"F2.wireOp",EDGE,"E32.4.0.3");var subQ1=sQuery(id+"F2.wireOp",EDGE,"E32.2.0.0");var subQ2=makeQuery(id+"F2.imprint","INTERSECT",VERTEX,{"derivedFrom":[subQ1,subQ0]});Q85=makeQuery(id+"F2.imprint","IMPRINT",FACE,{"disambiguationData":[TD([[makeQuery(id+"F2.imprint","IMPRINT",EDGE,{"disambiguationData":[TD([[subQ2,-1.0]])],"derivedFrom":subQ1}),1.0]])]});}
            var Q86;
            {var subQ0=sQuery(id+"F2.wireOp",EDGE,"E32.13.0.2");var subQ1=sQuery(id+"F2.wireOp",EDGE,"E32.13.0.0");var subQ2=makeQuery(id+"F2.imprint","INTERSECT",VERTEX,{"derivedFrom":[subQ1,subQ0]});Q86=makeQuery(id+"F2.imprint","IMPRINT",FACE,{"disambiguationData":[TD([[makeQuery(id+"F2.imprint","IMPRINT",EDGE,{"disambiguationData":[TD([[subQ2,1.0]])],"derivedFrom":subQ1}),-1.0]])]});}
            var Q87;
            {var subQ0=sQuery(id+"F2.wireOp",EDGE,"E32.9.0.3");var subQ1=sQuery(id+"F2.wireOp",EDGE,"E32.8.0.0");var subQ2=makeQuery(id+"F2.imprint","INTERSECT",VERTEX,{"derivedFrom":[subQ1,subQ0]});Q87=makeQuery(id+"F2.imprint","IMPRINT",FACE,{"disambiguationData":[TD([[makeQuery(id+"F2.imprint","IMPRINT",EDGE,{"disambiguationData":[TD([[subQ2,-1.0]])],"derivedFrom":subQ1}),1.0]])]});}
            var Q88;
            {var subQ0=sQuery(id+"F2.wireOp",EDGE,"E32.5.0.3");var subQ1=sQuery(id+"F2.wireOp",EDGE,"E32.2.0.0");var subQ2=makeQuery(id+"F2.imprint","INTERSECT",VERTEX,{"derivedFrom":[subQ1,subQ0]});Q88=makeQuery(id+"F2.imprint","IMPRINT",FACE,{"disambiguationData":[TD([[makeQuery(id+"F2.imprint","IMPRINT",EDGE,{"disambiguationData":[TD([[subQ2,-1.0]])],"derivedFrom":subQ1}),1.0]])]});}
            var Q89;
            {var subQ0=sQuery(id+"F2.wireOp",EDGE,"E32.15.0.3");var subQ1=sQuery(id+"F2.wireOp",EDGE,"E32.14.0.0");var subQ2=makeQuery(id+"F2.imprint","INTERSECT",VERTEX,{"derivedFrom":[subQ1,subQ0]});Q89=makeQuery(id+"F2.imprint","IMPRINT",FACE,{"disambiguationData":[TD([[makeQuery(id+"F2.imprint","IMPRINT",EDGE,{"disambiguationData":[TD([[subQ2,-1.0]])],"derivedFrom":subQ1}),1.0]])]});}
            var Q90;
            {var subQ0=sQuery(id+"F2.wireOp",EDGE,"E32.3.0.2");var subQ1=sQuery(id+"F2.wireOp",EDGE,"E32.3.0.0");var subQ2=makeQuery(id+"F2.imprint","INTERSECT",VERTEX,{"derivedFrom":[subQ1,subQ0]});Q90=makeQuery(id+"F2.imprint","IMPRINT",FACE,{"disambiguationData":[TD([[makeQuery(id+"F2.imprint","IMPRINT",EDGE,{"disambiguationData":[TD([[subQ2,1.0]])],"derivedFrom":subQ1}),-1.0]])]});}
            var Q91;
            {var subQ0=sQuery(id+"F2.wireOp",EDGE,"E31.2");var subQ1=sQuery(id+"F2.wireOp",EDGE,"E31.1");var subQ2=makeQuery(id+"F2.imprint","INTERSECT",VERTEX,{"derivedFrom":[subQ1,subQ0]});Q91=makeQuery(id+"F2.imprint","IMPRINT",FACE,{"disambiguationData":[TD([[makeQuery(id+"F2.imprint","IMPRINT",EDGE,{"disambiguationData":[TD([[subQ2,1.0]])],"derivedFrom":subQ1}),-1.0]])]});}
            var Q92;
            {var subQ0=sQuery(id+"F2.wireOp",EDGE,"E32.10.0.2");var subQ1=sQuery(id+"F2.wireOp",EDGE,"E32.10.0.0");var subQ2=makeQuery(id+"F2.imprint","INTERSECT",VERTEX,{"derivedFrom":[subQ1,subQ0]});Q92=makeQuery(id+"F2.imprint","IMPRINT",FACE,{"disambiguationData":[TD([[makeQuery(id+"F2.imprint","IMPRINT",EDGE,{"disambiguationData":[TD([[subQ2,1.0]])],"derivedFrom":subQ1}),-1.0]])]});}
            var Q93;
            {var subQ0=sQuery(id+"F2.wireOp",EDGE,"E32.6.0.3");var subQ1=sQuery(id+"F2.wireOp",EDGE,"E32.5.0.0");var subQ2=makeQuery(id+"F2.imprint","INTERSECT",VERTEX,{"derivedFrom":[subQ1,subQ0]});Q93=makeQuery(id+"F2.imprint","IMPRINT",FACE,{"disambiguationData":[TD([[makeQuery(id+"F2.imprint","IMPRINT",EDGE,{"disambiguationData":[TD([[subQ2,-1.0]])],"derivedFrom":subQ1}),1.0]])]});}
            var Q94;
            {var subQ0=sQuery(id+"F2.wireOp",EDGE,"E32.10.0.3");var subQ1=sQuery(id+"F2.wireOp",EDGE,"E32.9.0.0");var subQ2=makeQuery(id+"F2.imprint","INTERSECT",VERTEX,{"derivedFrom":[subQ1,subQ0]});Q94=makeQuery(id+"F2.imprint","IMPRINT",FACE,{"disambiguationData":[TD([[makeQuery(id+"F2.imprint","IMPRINT",EDGE,{"disambiguationData":[TD([[subQ2,-1.0]])],"derivedFrom":subQ1}),1.0]])]});}
            var Q95;
            {var subQ0=sQuery(id+"F2.wireOp",EDGE,"E32.5.0.3");var subQ1=sQuery(id+"F2.wireOp",EDGE,"E32.3.0.0");var subQ2=makeQuery(id+"F2.imprint","INTERSECT",VERTEX,{"derivedFrom":[subQ1,subQ0]});Q95=makeQuery(id+"F2.imprint","IMPRINT",FACE,{"disambiguationData":[TD([[makeQuery(id+"F2.imprint","IMPRINT",EDGE,{"disambiguationData":[TD([[subQ2,-1.0]])],"derivedFrom":subQ1}),1.0]])]});}
            var Q96;
            {var subQ0=sQuery(id+"F2.wireOp",EDGE,"E32.1.0.3");var subQ1=sQuery(id+"F2.wireOp",EDGE,"E31.1");var subQ2=makeQuery(id+"F2.imprint","INTERSECT",VERTEX,{"derivedFrom":[subQ1,subQ0]});Q96=makeQuery(id+"F2.imprint","IMPRINT",FACE,{"disambiguationData":[TD([[makeQuery(id+"F2.imprint","IMPRINT",EDGE,{"disambiguationData":[TD([[subQ2,-1.0]])],"derivedFrom":subQ1}),1.0]])]});}
            var Q97;
            {var subQ0=sQuery(id+"F2.wireOp",EDGE,"E32.9.0.2");var subQ1=sQuery(id+"F2.wireOp",EDGE,"E32.9.0.0");var subQ2=makeQuery(id+"F2.imprint","INTERSECT",VERTEX,{"derivedFrom":[subQ1,subQ0]});Q97=makeQuery(id+"F2.imprint","IMPRINT",FACE,{"disambiguationData":[TD([[makeQuery(id+"F2.imprint","IMPRINT",EDGE,{"disambiguationData":[TD([[subQ2,1.0]])],"derivedFrom":subQ1}),-1.0]])]});}
            var Q98;
            {var subQ0=sQuery(id+"F2.wireOp",EDGE,"E32.2.0.3");var subQ1=sQuery(id+"F2.wireOp",EDGE,"E32.1.0.0");var subQ2=makeQuery(id+"F2.imprint","INTERSECT",VERTEX,{"derivedFrom":[subQ1,subQ0]});Q98=makeQuery(id+"F2.imprint","IMPRINT",FACE,{"disambiguationData":[TD([[makeQuery(id+"F2.imprint","IMPRINT",EDGE,{"disambiguationData":[TD([[subQ2,-1.0]])],"derivedFrom":subQ1}),1.0]])]});}
            var Q99;
            {var subQ0=sQuery(id+"F2.wireOp",EDGE,"E32.5.0.2");var subQ1=sQuery(id+"F2.wireOp",EDGE,"E32.5.0.0");var subQ2=makeQuery(id+"F2.imprint","INTERSECT",VERTEX,{"derivedFrom":[subQ1,subQ0]});Q99=makeQuery(id+"F2.imprint","IMPRINT",FACE,{"disambiguationData":[TD([[makeQuery(id+"F2.imprint","IMPRINT",EDGE,{"disambiguationData":[TD([[subQ2,1.0]])],"derivedFrom":subQ1}),-1.0]])]});}
            var Q100;
            {var subQ0=sQuery(id+"F2.wireOp",EDGE,"E32.3.0.3");var subQ1=sQuery(id+"F2.wireOp",EDGE,"E31.1");var subQ2=makeQuery(id+"F2.imprint","INTERSECT",VERTEX,{"derivedFrom":[subQ1,subQ0]});Q100=makeQuery(id+"F2.imprint","IMPRINT",FACE,{"disambiguationData":[TD([[makeQuery(id+"F2.imprint","IMPRINT",EDGE,{"disambiguationData":[TD([[subQ2,-1.0]])],"derivedFrom":subQ1}),1.0]])]});}
            var Q101;
            {var subQ0=sQuery(id+"F2.wireOp",EDGE,"E32.2.0.3");var subQ1=sQuery(id+"F2.wireOp",EDGE,"E31.1");var subQ2=makeQuery(id+"F2.imprint","INTERSECT",VERTEX,{"derivedFrom":[subQ1,subQ0]});Q101=makeQuery(id+"F2.imprint","IMPRINT",FACE,{"disambiguationData":[TD([[makeQuery(id+"F2.imprint","IMPRINT",EDGE,{"disambiguationData":[TD([[subQ2,-1.0]])],"derivedFrom":subQ1}),1.0]])]});}
            var Q102;
            {var subQ0=sQuery(id+"F2.wireOp",EDGE,"E32.10.0.3");var subQ1=sQuery(id+"F2.wireOp",EDGE,"E32.7.0.0");var subQ2=makeQuery(id+"F2.imprint","INTERSECT",VERTEX,{"derivedFrom":[subQ1,subQ0]});Q102=makeQuery(id+"F2.imprint","IMPRINT",FACE,{"disambiguationData":[TD([[makeQuery(id+"F2.imprint","IMPRINT",EDGE,{"disambiguationData":[TD([[subQ2,-1.0]])],"derivedFrom":subQ1}),1.0]])]});}
            var Q103;
            {var subQ0=sQuery(id+"F2.wireOp",EDGE,"E32.6.0.3");var subQ1=sQuery(id+"F2.wireOp",EDGE,"E32.4.0.0");var subQ2=makeQuery(id+"F2.imprint","INTERSECT",VERTEX,{"derivedFrom":[subQ1,subQ0]});Q103=makeQuery(id+"F2.imprint","IMPRINT",FACE,{"disambiguationData":[TD([[makeQuery(id+"F2.imprint","IMPRINT",EDGE,{"disambiguationData":[TD([[subQ2,-1.0]])],"derivedFrom":subQ1}),1.0]])]});}
            var Q104;
            {var subQ0=sQuery(id+"F2.wireOp",EDGE,"E32.11.0.2");var subQ1=sQuery(id+"F2.wireOp",EDGE,"E32.11.0.0");var subQ2=makeQuery(id+"F2.imprint","INTERSECT",VERTEX,{"derivedFrom":[subQ1,subQ0]});Q104=makeQuery(id+"F2.imprint","IMPRINT",FACE,{"disambiguationData":[TD([[makeQuery(id+"F2.imprint","IMPRINT",EDGE,{"disambiguationData":[TD([[subQ2,1.0]])],"derivedFrom":subQ1}),-1.0]])]});}
            var Q105;
            {var subQ0=sQuery(id+"F2.wireOp",EDGE,"E32.7.0.3");var subQ1=sQuery(id+"F2.wireOp",EDGE,"E32.5.0.0");var subQ2=makeQuery(id+"F2.imprint","INTERSECT",VERTEX,{"derivedFrom":[subQ1,subQ0]});Q105=makeQuery(id+"F2.imprint","IMPRINT",FACE,{"disambiguationData":[TD([[makeQuery(id+"F2.imprint","IMPRINT",EDGE,{"disambiguationData":[TD([[subQ2,-1.0]])],"derivedFrom":subQ1}),1.0]])]});}
            var Q106;
            {var subQ0=sQuery(id+"F2.wireOp",EDGE,"E32.3.0.3");var subQ1=sQuery(id+"F2.wireOp",EDGE,"E32.1.0.0");var subQ2=makeQuery(id+"F2.imprint","INTERSECT",VERTEX,{"derivedFrom":[subQ1,subQ0]});Q106=makeQuery(id+"F2.imprint","IMPRINT",FACE,{"disambiguationData":[TD([[makeQuery(id+"F2.imprint","IMPRINT",EDGE,{"disambiguationData":[TD([[subQ2,-1.0]])],"derivedFrom":subQ1}),1.0]])]});}
            var Q107;
            {var subQ0=sQuery(id+"F2.wireOp",EDGE,"E32.15.0.3");var subQ1=sQuery(id+"F2.wireOp",EDGE,"E32.13.0.0");var subQ2=makeQuery(id+"F2.imprint","INTERSECT",VERTEX,{"derivedFrom":[subQ1,subQ0]});Q107=makeQuery(id+"F2.imprint","IMPRINT",FACE,{"disambiguationData":[TD([[makeQuery(id+"F2.imprint","IMPRINT",EDGE,{"disambiguationData":[TD([[subQ2,-1.0]])],"derivedFrom":subQ1}),1.0]])]});}
            var Q108;
            {var subQ0=sQuery(id+"F2.wireOp",EDGE,"E32.13.0.3");var subQ1=sQuery(id+"F2.wireOp",EDGE,"E32.12.0.0");var subQ2=makeQuery(id+"F2.imprint","INTERSECT",VERTEX,{"derivedFrom":[subQ1,subQ0]});Q108=makeQuery(id+"F2.imprint","IMPRINT",FACE,{"disambiguationData":[TD([[makeQuery(id+"F2.imprint","IMPRINT",EDGE,{"disambiguationData":[TD([[subQ2,-1.0]])],"derivedFrom":subQ1}),1.0]])]});}
            var Q109;
            {var subQ0=sQuery(id+"F2.wireOp",EDGE,"E32.12.0.3");var subQ1=sQuery(id+"F2.wireOp",EDGE,"E32.9.0.0");var subQ2=makeQuery(id+"F2.imprint","INTERSECT",VERTEX,{"derivedFrom":[subQ1,subQ0]});Q109=makeQuery(id+"F2.imprint","IMPRINT",FACE,{"disambiguationData":[TD([[makeQuery(id+"F2.imprint","IMPRINT",EDGE,{"disambiguationData":[TD([[subQ2,-1.0]])],"derivedFrom":subQ1}),1.0]])]});}
            var Q110;
            {var subQ0=sQuery(id+"F2.wireOp",EDGE,"E32.12.0.2");var subQ1=sQuery(id+"F2.wireOp",EDGE,"E32.12.0.0");var subQ2=makeQuery(id+"F2.imprint","INTERSECT",VERTEX,{"derivedFrom":[subQ1,subQ0]});Q110=makeQuery(id+"F2.imprint","IMPRINT",FACE,{"disambiguationData":[TD([[makeQuery(id+"F2.imprint","IMPRINT",EDGE,{"disambiguationData":[TD([[subQ2,1.0]])],"derivedFrom":subQ1}),-1.0]])]});}
            var Q111;
            {var subQ0=sQuery(id+"F2.wireOp",EDGE,"E32.14.0.3");var subQ1=sQuery(id+"F2.wireOp",EDGE,"E32.13.0.0");var subQ2=makeQuery(id+"F2.imprint","INTERSECT",VERTEX,{"derivedFrom":[subQ1,subQ0]});Q111=makeQuery(id+"F2.imprint","IMPRINT",FACE,{"disambiguationData":[TD([[makeQuery(id+"F2.imprint","IMPRINT",EDGE,{"disambiguationData":[TD([[subQ2,-1.0]])],"derivedFrom":subQ1}),1.0]])]});}
            var Q112;
            {var subQ0=sQuery(id+"F2.wireOp",EDGE,"E32.8.0.3");var subQ1=sQuery(id+"F2.wireOp",EDGE,"E32.6.0.0");var subQ2=makeQuery(id+"F2.imprint","INTERSECT",VERTEX,{"derivedFrom":[subQ1,subQ0]});Q112=makeQuery(id+"F2.imprint","IMPRINT",FACE,{"disambiguationData":[TD([[makeQuery(id+"F2.imprint","IMPRINT",EDGE,{"disambiguationData":[TD([[subQ2,-1.0]])],"derivedFrom":subQ1}),1.0]])]});}
            var Q113;
            {var subQ0=sQuery(id+"F2.wireOp",EDGE,"E32.13.0.3");var subQ1=sQuery(id+"F2.wireOp",EDGE,"E32.10.0.0");var subQ2=makeQuery(id+"F2.imprint","INTERSECT",VERTEX,{"derivedFrom":[subQ1,subQ0]});Q113=makeQuery(id+"F2.imprint","IMPRINT",FACE,{"disambiguationData":[TD([[makeQuery(id+"F2.imprint","IMPRINT",EDGE,{"disambiguationData":[TD([[subQ2,-1.0]])],"derivedFrom":subQ1}),1.0]])]});}
            var Q114;
            {var subQ0=sQuery(id+"F2.wireOp",EDGE,"E32.9.0.3");var subQ1=sQuery(id+"F2.wireOp",EDGE,"E32.6.0.0");var subQ2=makeQuery(id+"F2.imprint","INTERSECT",VERTEX,{"derivedFrom":[subQ1,subQ0]});Q114=makeQuery(id+"F2.imprint","IMPRINT",FACE,{"disambiguationData":[TD([[makeQuery(id+"F2.imprint","IMPRINT",EDGE,{"disambiguationData":[TD([[subQ2,-1.0]])],"derivedFrom":subQ1}),1.0]])]});}
            var Q115;
            {var subQ0=sQuery(id+"F2.wireOp",EDGE,"E32.16.0.3");var subQ1=sQuery(id+"F2.wireOp",EDGE,"E32.14.0.0");var subQ2=makeQuery(id+"F2.imprint","INTERSECT",VERTEX,{"derivedFrom":[subQ1,subQ0]});Q115=makeQuery(id+"F2.imprint","IMPRINT",FACE,{"disambiguationData":[TD([[makeQuery(id+"F2.imprint","IMPRINT",EDGE,{"disambiguationData":[TD([[subQ2,-1.0]])],"derivedFrom":subQ1}),1.0]])]});}
            var Q116;
            {var subQ0=sQuery(id+"F2.wireOp",EDGE,"E32.4.0.3");var subQ1=sQuery(id+"F2.wireOp",EDGE,"E32.3.0.0");var subQ2=makeQuery(id+"F2.imprint","INTERSECT",VERTEX,{"derivedFrom":[subQ1,subQ0]});Q116=makeQuery(id+"F2.imprint","IMPRINT",FACE,{"disambiguationData":[TD([[makeQuery(id+"F2.imprint","IMPRINT",EDGE,{"disambiguationData":[TD([[subQ2,-1.0]])],"derivedFrom":subQ1}),1.0]])]});}
            var Q117;
            {var subQ0=sQuery(id+"F2.wireOp",EDGE,"E32.2.0.2");var subQ1=sQuery(id+"F2.wireOp",EDGE,"E32.2.0.0");var subQ2=makeQuery(id+"F2.imprint","INTERSECT",VERTEX,{"derivedFrom":[subQ1,subQ0]});Q117=makeQuery(id+"F2.imprint","IMPRINT",FACE,{"disambiguationData":[TD([[makeQuery(id+"F2.imprint","IMPRINT",EDGE,{"disambiguationData":[TD([[subQ2,1.0]])],"derivedFrom":subQ1}),-1.0]])]});}
            var Q118;
            {var subQ0=sQuery(id+"F2.wireOp",EDGE,"E32.5.0.3");var subQ1=sQuery(id+"F2.wireOp",EDGE,"E32.4.0.0");var subQ2=makeQuery(id+"F2.imprint","INTERSECT",VERTEX,{"derivedFrom":[subQ1,subQ0]});Q118=makeQuery(id+"F2.imprint","IMPRINT",FACE,{"disambiguationData":[TD([[makeQuery(id+"F2.imprint","IMPRINT",EDGE,{"disambiguationData":[TD([[subQ2,-1.0]])],"derivedFrom":subQ1}),1.0]])]});}
            var Q119;
            {var subQ0=sQuery(id+"F2.wireOp",EDGE,"E32.3.0.3");var subQ1=sQuery(id+"F2.wireOp",EDGE,"E32.2.0.0");var subQ2=makeQuery(id+"F2.imprint","INTERSECT",VERTEX,{"derivedFrom":[subQ1,subQ0]});Q119=makeQuery(id+"F2.imprint","IMPRINT",FACE,{"disambiguationData":[TD([[makeQuery(id+"F2.imprint","IMPRINT",EDGE,{"disambiguationData":[TD([[subQ2,-1.0]])],"derivedFrom":subQ1}),1.0]])]});}
            var Q120;
            {var subQ0=sQuery(id+"F2.wireOp",EDGE,"E32.1.0.2");var subQ1=sQuery(id+"F2.wireOp",EDGE,"E32.1.0.0");var subQ2=makeQuery(id+"F2.imprint","INTERSECT",VERTEX,{"derivedFrom":[subQ1,subQ0]});Q120=makeQuery(id+"F2.imprint","IMPRINT",FACE,{"disambiguationData":[TD([[makeQuery(id+"F2.imprint","IMPRINT",EDGE,{"disambiguationData":[TD([[subQ2,1.0]])],"derivedFrom":subQ1}),-1.0]])]});}
            var Q121;
            {var subQ0=sQuery(id+"F2.wireOp",EDGE,"E32.11.0.3");var subQ1=sQuery(id+"F2.wireOp",EDGE,"E32.8.0.0");var subQ2=makeQuery(id+"F2.imprint","INTERSECT",VERTEX,{"derivedFrom":[subQ1,subQ0]});Q121=makeQuery(id+"F2.imprint","IMPRINT",FACE,{"disambiguationData":[TD([[makeQuery(id+"F2.imprint","IMPRINT",EDGE,{"disambiguationData":[TD([[subQ2,-1.0]])],"derivedFrom":subQ1}),1.0]])]});}
            var Q122;
            {var subQ0=sQuery(id+"F2.wireOp",EDGE,"E32.11.0.3");var subQ1=sQuery(id+"F2.wireOp",EDGE,"E32.9.0.0");var subQ2=makeQuery(id+"F2.imprint","INTERSECT",VERTEX,{"derivedFrom":[subQ1,subQ0]});Q122=makeQuery(id+"F2.imprint","IMPRINT",FACE,{"disambiguationData":[TD([[makeQuery(id+"F2.imprint","IMPRINT",EDGE,{"disambiguationData":[TD([[subQ2,-1.0]])],"derivedFrom":subQ1}),1.0]])]});}
            var Q123;
            {var subQ0=sQuery(id+"F2.wireOp",EDGE,"E32.12.0.3");var subQ1=sQuery(id+"F2.wireOp",EDGE,"E32.10.0.0");var subQ2=makeQuery(id+"F2.imprint","INTERSECT",VERTEX,{"derivedFrom":[subQ1,subQ0]});Q123=makeQuery(id+"F2.imprint","IMPRINT",FACE,{"disambiguationData":[TD([[makeQuery(id+"F2.imprint","IMPRINT",EDGE,{"disambiguationData":[TD([[subQ2,-1.0]])],"derivedFrom":subQ1}),1.0]])]});}
            var Q124;
            {var subQ0=sQuery(id+"F2.wireOp",EDGE,"E32.10.0.3");var subQ1=sQuery(id+"F2.wireOp",EDGE,"E32.8.0.0");var subQ2=makeQuery(id+"F2.imprint","INTERSECT",VERTEX,{"derivedFrom":[subQ1,subQ0]});Q124=makeQuery(id+"F2.imprint","IMPRINT",FACE,{"disambiguationData":[TD([[makeQuery(id+"F2.imprint","IMPRINT",EDGE,{"disambiguationData":[TD([[subQ2,-1.0]])],"derivedFrom":subQ1}),1.0]])]});}
            var Q125;
            {var subQ0=sQuery(id+"F2.wireOp",EDGE,"E104.MirrorCS");var subQ5=sQuery(id+"F2.wireOp",EDGE,"E46.MirrorCS");var subQ6=makeQuery(id+"F2.imprint","INTERSECT",VERTEX,{"derivedFrom":[subQ5,subQ0]});Q125=makeQuery(id+"F2.imprint","IMPRINT",FACE,{"disambiguationData":[TD([[makeQuery(id+"F2.imprint","IMPRINT",EDGE,{"disambiguationData":[TD([[subQ6,1.0]])],"derivedFrom":subQ5}),1.0]])]});}
            var Q126;
            {var subQ0=sQuery(id+"F2.wireOp",EDGE,"E55.MirrorCS");var subQ1=sQuery(id+"F2.wireOp",EDGE,"E53.MirrorCS");var subQ2=makeQuery(id+"F2.imprint","INTERSECT",VERTEX,{"derivedFrom":[subQ1,subQ0]});Q126=makeQuery(id+"F2.imprint","IMPRINT",FACE,{"disambiguationData":[TD([[makeQuery(id+"F2.imprint","IMPRINT",EDGE,{"disambiguationData":[TD([[subQ2,1.0]])],"derivedFrom":subQ1}),1.0]])]});}
            var Q127;
            {var subQ0=sQuery(id+"F2.wireOp",EDGE,"E87.MirrorCS");var subQ1=sQuery(id+"F2.wireOp",EDGE,"E56.MirrorCS");var subQ2=makeQuery(id+"F2.imprint","INTERSECT",VERTEX,{"derivedFrom":[subQ1,subQ0]});Q127=makeQuery(id+"F2.imprint","IMPRINT",FACE,{"disambiguationData":[TD([[makeQuery(id+"F2.imprint","IMPRINT",EDGE,{"disambiguationData":[TD([[subQ2,-1.0]])],"derivedFrom":subQ1}),-1.0]])]});}
            var Q128;
            {var subQ0=sQuery(id+"F2.wireOp",EDGE,"E102.MirrorCS");var subQ1=sQuery(id+"F2.wireOp",EDGE,"E53.MirrorCS");var subQ2=makeQuery(id+"F2.imprint","INTERSECT",VERTEX,{"derivedFrom":[subQ1,subQ0]});Q128=makeQuery(id+"F2.imprint","IMPRINT",FACE,{"disambiguationData":[TD([[makeQuery(id+"F2.imprint","IMPRINT",EDGE,{"disambiguationData":[TD([[subQ2,1.0]])],"derivedFrom":subQ1}),-1.0]])]});}
            var Q129;
            {var subQ0=sQuery(id+"F2.wireOp",EDGE,"E66.MirrorCS");var subQ1=sQuery(id+"F2.wireOp",EDGE,"E57.MirrorCS");var subQ2=makeQuery(id+"F2.imprint","INTERSECT",VERTEX,{"derivedFrom":[subQ1,subQ0]});Q129=makeQuery(id+"F2.imprint","IMPRINT",FACE,{"disambiguationData":[TD([[makeQuery(id+"F2.imprint","IMPRINT",EDGE,{"disambiguationData":[TD([[subQ2,1.0]])],"derivedFrom":subQ1}),-1.0]])]});}
            var Q130;
            {var subQ0=sQuery(id+"F2.wireOp",EDGE,"E85.MirrorCS");var subQ1=sQuery(id+"F2.wireOp",EDGE,"E57.MirrorCS");var subQ2=makeQuery(id+"F2.imprint","INTERSECT",VERTEX,{"derivedFrom":[subQ1,subQ0]});Q130=makeQuery(id+"F2.imprint","IMPRINT",FACE,{"disambiguationData":[TD([[makeQuery(id+"F2.imprint","IMPRINT",EDGE,{"disambiguationData":[TD([[subQ2,1.0]])],"derivedFrom":subQ1}),1.0]])]});}
            var Q131;
            {var subQ0=sQuery(id+"F2.wireOp",EDGE,"E77.MirrorCS");var subQ1=sQuery(id+"F2.wireOp",EDGE,"E58.MirrorCS");var subQ2=makeQuery(id+"F2.imprint","INTERSECT",VERTEX,{"derivedFrom":[subQ1,subQ0]});Q131=makeQuery(id+"F2.imprint","IMPRINT",FACE,{"disambiguationData":[TD([[makeQuery(id+"F2.imprint","IMPRINT",EDGE,{"disambiguationData":[TD([[subQ2,1.0]])],"derivedFrom":subQ1}),-1.0]])]});}
            var Q132;
            {var subQ0=sQuery(id+"F2.wireOp",EDGE,"E106.MirrorCS");var subQ1=sQuery(id+"F2.wireOp",EDGE,"E58.MirrorCS");var subQ2=makeQuery(id+"F2.imprint","INTERSECT",VERTEX,{"derivedFrom":[subQ1,subQ0]});Q132=makeQuery(id+"F2.imprint","IMPRINT",FACE,{"disambiguationData":[TD([[makeQuery(id+"F2.imprint","IMPRINT",EDGE,{"disambiguationData":[TD([[subQ2,1.0]])],"derivedFrom":subQ1}),1.0]])]});}
            var Q133;
            {var subQ0=sQuery(id+"F2.wireOp",EDGE,"E104.MirrorCS");var subQ1=sQuery(id+"F2.wireOp",EDGE,"E61.MirrorCS");var subQ2=makeQuery(id+"F2.imprint","INTERSECT",VERTEX,{"derivedFrom":[subQ1,subQ0]});Q133=makeQuery(id+"F2.imprint","IMPRINT",FACE,{"disambiguationData":[TD([[makeQuery(id+"F2.imprint","IMPRINT",EDGE,{"disambiguationData":[TD([[subQ2,-1.0]])],"derivedFrom":subQ1}),-1.0]])]});}
            var Q134;
            {var subQ0=sQuery(id+"F2.wireOp",EDGE,"E93.MirrorCS");var subQ1=sQuery(id+"F2.wireOp",EDGE,"E71.MirrorCS");var subQ2=makeQuery(id+"F2.imprint","INTERSECT",VERTEX,{"derivedFrom":[subQ1,subQ0]});Q134=makeQuery(id+"F2.imprint","IMPRINT",FACE,{"disambiguationData":[TD([[makeQuery(id+"F2.imprint","IMPRINT",EDGE,{"disambiguationData":[TD([[subQ2,1.0]])],"derivedFrom":subQ1}),-1.0]])]});}
            var Q135;
            {var subQ0=sQuery(id+"F2.wireOp",EDGE,"E74.MirrorCS");var subQ1=sQuery(id+"F2.wireOp",EDGE,"E55.MirrorCS");var subQ2=makeQuery(id+"F2.imprint","INTERSECT",VERTEX,{"derivedFrom":[subQ1,subQ0]});Q135=makeQuery(id+"F2.imprint","IMPRINT",FACE,{"disambiguationData":[TD([[makeQuery(id+"F2.imprint","IMPRINT",EDGE,{"disambiguationData":[TD([[subQ2,-1.0]])],"derivedFrom":subQ1}),-1.0]])]});}
            var Q136;
            {var subQ1=sQuery(id+"F2.wireOp",EDGE,"E37.MirrorCS");Q136=makeQuery(id+"F2.imprint","IMPRINT",FACE,{"disambiguationData":[TD([[makeQuery(id+"F2.imprint","IMPRINT",EDGE,{"derivedFrom":subQ1}),1.0]])]});}
            var Q137;
            {var subQ0=sQuery(id+"F2.wireOp",EDGE,"E100.MirrorCS");var subQ1=sQuery(id+"F2.wireOp",EDGE,"E71.MirrorCS");var subQ2=makeQuery(id+"F2.imprint","INTERSECT",VERTEX,{"derivedFrom":[subQ1,subQ0]});Q137=makeQuery(id+"F2.imprint","IMPRINT",FACE,{"disambiguationData":[TD([[makeQuery(id+"F2.imprint","IMPRINT",EDGE,{"disambiguationData":[TD([[subQ2,1.0]])],"derivedFrom":subQ1}),1.0]])]});}
            var Q138;
            {var subQ0=sQuery(id+"F2.wireOp",EDGE,"E69.MirrorCS");Q138=makeQuery(id+"F2.imprint","IMPRINT",FACE,{"disambiguationData":[TD([[makeQuery(id+"F2.imprint","IMPRINT",EDGE,{"derivedFrom":subQ0}),1.0]])]});}
            var Q139;
            {var subQ0=sQuery(id+"F2.wireOp",EDGE,"E72.MirrorCS");var subQ1=sQuery(id+"F2.wireOp",EDGE,"E56.MirrorCS");var subQ2=makeQuery(id+"F2.imprint","INTERSECT",VERTEX,{"derivedFrom":[subQ1,subQ0]});Q139=makeQuery(id+"F2.imprint","IMPRINT",FACE,{"disambiguationData":[TD([[makeQuery(id+"F2.imprint","IMPRINT",EDGE,{"disambiguationData":[TD([[subQ2,-1.0]])],"derivedFrom":subQ1}),1.0]])]});}
            var Q140;
            {var subQ0=sQuery(id+"F2.wireOp",EDGE,"E77.MirrorCS");var subQ1=sQuery(id+"F2.wireOp",EDGE,"E57.MirrorCS");var subQ2=makeQuery(id+"F2.imprint","INTERSECT",VERTEX,{"derivedFrom":[subQ1,subQ0]});Q140=makeQuery(id+"F2.imprint","IMPRINT",FACE,{"disambiguationData":[TD([[makeQuery(id+"F2.imprint","IMPRINT",EDGE,{"disambiguationData":[TD([[subQ2,-1.0]])],"derivedFrom":subQ1}),-1.0]])]});}
            var Q141;
            {var subQ0=sQuery(id+"F2.wireOp",EDGE,"E95.MirrorCS");var subQ1=sQuery(id+"F2.wireOp",EDGE,"E68.MirrorCS");var subQ2=makeQuery(id+"F2.imprint","INTERSECT",VERTEX,{"derivedFrom":[subQ1,subQ0]});Q141=makeQuery(id+"F2.imprint","IMPRINT",FACE,{"disambiguationData":[TD([[makeQuery(id+"F2.imprint","IMPRINT",EDGE,{"disambiguationData":[TD([[subQ2,1.0]])],"derivedFrom":subQ1}),-1.0]])]});}
            var Q142;
            {var subQ0=sQuery(id+"F2.wireOp",EDGE,"E93.MirrorCS");var subQ1=sQuery(id+"F2.wireOp",EDGE,"E71.MirrorCS");var subQ2=makeQuery(id+"F2.imprint","INTERSECT",VERTEX,{"derivedFrom":[subQ1,subQ0]});Q142=makeQuery(id+"F2.imprint","IMPRINT",FACE,{"disambiguationData":[TD([[makeQuery(id+"F2.imprint","IMPRINT",EDGE,{"disambiguationData":[TD([[subQ2,1.0]])],"derivedFrom":subQ1}),1.0]])]});}
            var Q143;
            {var subQ0=sQuery(id+"F2.wireOp",EDGE,"E77.MirrorCS");var subQ1=sQuery(id+"F2.wireOp",EDGE,"E57.MirrorCS");var subQ2=makeQuery(id+"F2.imprint","INTERSECT",VERTEX,{"derivedFrom":[subQ1,subQ0]});Q143=makeQuery(id+"F2.imprint","IMPRINT",FACE,{"disambiguationData":[TD([[makeQuery(id+"F2.imprint","IMPRINT",EDGE,{"disambiguationData":[TD([[subQ2,-1.0]])],"derivedFrom":subQ1}),1.0]])]});}
            var Q144;
            {var subQ0=sQuery(id+"F2.wireOp",EDGE,"E89.MirrorCS");var subQ1=sQuery(id+"F2.wireOp",EDGE,"E71.MirrorCS");var subQ2=makeQuery(id+"F2.imprint","INTERSECT",VERTEX,{"derivedFrom":[subQ1,subQ0]});Q144=makeQuery(id+"F2.imprint","IMPRINT",FACE,{"disambiguationData":[TD([[makeQuery(id+"F2.imprint","IMPRINT",EDGE,{"disambiguationData":[TD([[subQ2,-1.0]])],"derivedFrom":subQ1}),1.0]])]});}
            var Q145;
            {var subQ0=sQuery(id+"F2.wireOp",EDGE,"E96.MirrorCS");var subQ1=sQuery(id+"F2.wireOp",EDGE,"E56.MirrorCS");var subQ2=makeQuery(id+"F2.imprint","INTERSECT",VERTEX,{"derivedFrom":[subQ1,subQ0]});Q145=makeQuery(id+"F2.imprint","IMPRINT",FACE,{"disambiguationData":[TD([[makeQuery(id+"F2.imprint","IMPRINT",EDGE,{"disambiguationData":[TD([[subQ2,-1.0]])],"derivedFrom":subQ1}),-1.0]])]});}
            var Q146;
            {var subQ0=sQuery(id+"F2.wireOp",EDGE,"E61.MirrorCS");var subQ1=sQuery(id+"F2.wireOp",EDGE,"E53.MirrorCS");var subQ2=makeQuery(id+"F2.imprint","INTERSECT",VERTEX,{"derivedFrom":[subQ1,subQ0]});Q146=makeQuery(id+"F2.imprint","IMPRINT",FACE,{"disambiguationData":[TD([[makeQuery(id+"F2.imprint","IMPRINT",EDGE,{"disambiguationData":[TD([[subQ2,-1.0]])],"derivedFrom":subQ1}),1.0]])]});}
            var Q147;
            {var subQ1=sQuery(id+"F2.wireOp",EDGE,"E53.MirrorCS");var subQ7=sQuery(id+"F2.wireOp",EDGE,"E41.MirrorCS");var subQ8=makeQuery(id+"F2.imprint","INTERSECT",VERTEX,{"derivedFrom":[subQ7,subQ1]});Q147=makeQuery(id+"F2.imprint","IMPRINT",FACE,{"disambiguationData":[TD([[makeQuery(id+"F2.imprint","IMPRINT",EDGE,{"disambiguationData":[TD([[subQ8,1.0]])],"derivedFrom":subQ7}),-1.0]])]});}
            var Q148;
            {var subQ0=sQuery(id+"F2.wireOp",EDGE,"E102.MirrorCS");var subQ1=sQuery(id+"F2.wireOp",EDGE,"E53.MirrorCS");var subQ2=makeQuery(id+"F2.imprint","INTERSECT",VERTEX,{"derivedFrom":[subQ1,subQ0]});Q148=makeQuery(id+"F2.imprint","IMPRINT",FACE,{"disambiguationData":[TD([[makeQuery(id+"F2.imprint","IMPRINT",EDGE,{"disambiguationData":[TD([[subQ2,1.0]])],"derivedFrom":subQ1}),1.0]])]});}
            var Q149;
            {var subQ1=sQuery(id+"F2.wireOp",EDGE,"E53.MirrorCS");var subQ5=sQuery(id+"F2.wireOp",EDGE,"E41.MirrorCS");var subQ6=makeQuery(id+"F2.imprint","INTERSECT",VERTEX,{"derivedFrom":[subQ5,subQ1]});Q149=makeQuery(id+"F2.imprint","IMPRINT",FACE,{"disambiguationData":[TD([[makeQuery(id+"F2.imprint","IMPRINT",EDGE,{"disambiguationData":[TD([[subQ6,1.0]])],"derivedFrom":subQ5}),1.0]])]});}
            var Q150;
            {var subQ0=sQuery(id+"F2.wireOp",EDGE,"E56.MirrorCS");var subQ1=sQuery(id+"F2.wireOp",EDGE,"E54.MirrorCS");var subQ2=makeQuery(id+"F2.imprint","INTERSECT",VERTEX,{"derivedFrom":[subQ1,subQ0]});Q150=makeQuery(id+"F2.imprint","IMPRINT",FACE,{"disambiguationData":[TD([[makeQuery(id+"F2.imprint","IMPRINT",EDGE,{"disambiguationData":[TD([[subQ2,-1.0]])],"derivedFrom":subQ1}),-1.0]])]});}
            var Q151;
            {var subQ0=sQuery(id+"F2.wireOp",EDGE,"E66.MirrorCS");var subQ1=sQuery(id+"F2.wireOp",EDGE,"E57.MirrorCS");var subQ2=makeQuery(id+"F2.imprint","INTERSECT",VERTEX,{"derivedFrom":[subQ1,subQ0]});Q151=makeQuery(id+"F2.imprint","IMPRINT",FACE,{"disambiguationData":[TD([[makeQuery(id+"F2.imprint","IMPRINT",EDGE,{"disambiguationData":[TD([[subQ2,1.0]])],"derivedFrom":subQ1}),1.0]])]});}
            var Q152;
            {var subQ0=sQuery(id+"F2.wireOp",EDGE,"E79.MirrorCS");var subQ1=sQuery(id+"F2.wireOp",EDGE,"E54.MirrorCS");var subQ2=makeQuery(id+"F2.imprint","INTERSECT",VERTEX,{"derivedFrom":[subQ1,subQ0]});Q152=makeQuery(id+"F2.imprint","IMPRINT",FACE,{"disambiguationData":[TD([[makeQuery(id+"F2.imprint","IMPRINT",EDGE,{"disambiguationData":[TD([[subQ2,-1.0]])],"derivedFrom":subQ1}),-1.0]])]});}
            var Q153;
            {var subQ0=sQuery(id+"F2.wireOp",EDGE,"E74.MirrorCS");var subQ1=sQuery(id+"F2.wireOp",EDGE,"E55.MirrorCS");var subQ2=makeQuery(id+"F2.imprint","INTERSECT",VERTEX,{"derivedFrom":[subQ1,subQ0]});Q153=makeQuery(id+"F2.imprint","IMPRINT",FACE,{"disambiguationData":[TD([[makeQuery(id+"F2.imprint","IMPRINT",EDGE,{"disambiguationData":[TD([[subQ2,-1.0]])],"derivedFrom":subQ1}),1.0]])]});}
            var Q154;
            {var subQ0=sQuery(id+"F2.wireOp",EDGE,"E86.MirrorCS");var subQ1=sQuery(id+"F2.wireOp",EDGE,"E63.MirrorCS");var subQ2=makeQuery(id+"F2.imprint","INTERSECT",VERTEX,{"derivedFrom":[subQ1,subQ0]});Q154=makeQuery(id+"F2.imprint","IMPRINT",FACE,{"disambiguationData":[TD([[makeQuery(id+"F2.imprint","IMPRINT",EDGE,{"disambiguationData":[TD([[subQ2,-1.0]])],"derivedFrom":subQ1}),-1.0]])]});}
            var Q155;
            {var subQ5=sQuery(id+"F2.wireOp",EDGE,"E63.MirrorCS");var subQ6=sQuery(id+"F2.wireOp",EDGE,"E47.MirrorCS");var subQ7=makeQuery(id+"F2.imprint","INTERSECT",VERTEX,{"derivedFrom":[subQ6,subQ5]});Q155=makeQuery(id+"F2.imprint","IMPRINT",FACE,{"disambiguationData":[TD([[makeQuery(id+"F2.imprint","IMPRINT",EDGE,{"disambiguationData":[TD([[subQ7,1.0]])],"derivedFrom":subQ6}),-1.0]])]});}
            var Q156;
            {var subQ0=sQuery(id+"F2.wireOp",EDGE,"E72.MirrorCS");var subQ1=sQuery(id+"F2.wireOp",EDGE,"E66.MirrorCS");var subQ2=makeQuery(id+"F2.imprint","INTERSECT",VERTEX,{"derivedFrom":[subQ1,subQ0]});Q156=makeQuery(id+"F2.imprint","IMPRINT",FACE,{"disambiguationData":[TD([[makeQuery(id+"F2.imprint","IMPRINT",EDGE,{"disambiguationData":[TD([[subQ2,-1.0]])],"derivedFrom":subQ1}),1.0]])]});}
            var Q157;
            {var subQ0=sQuery(id+"F2.wireOp",EDGE,"E63.MirrorCS");var subQ1=sQuery(id+"F2.wireOp",EDGE,"E55.MirrorCS");var subQ2=makeQuery(id+"F2.imprint","INTERSECT",VERTEX,{"derivedFrom":[subQ1,subQ0]});Q157=makeQuery(id+"F2.imprint","IMPRINT",FACE,{"disambiguationData":[TD([[makeQuery(id+"F2.imprint","IMPRINT",EDGE,{"disambiguationData":[TD([[subQ2,-1.0]])],"derivedFrom":subQ1}),1.0]])]});}
            var Q158;
            {var subQ0=sQuery(id+"F2.wireOp",EDGE,"E103.MirrorCS");var subQ1=sQuery(id+"F2.wireOp",EDGE,"E60.MirrorCS");var subQ2=makeQuery(id+"F2.imprint","INTERSECT",VERTEX,{"derivedFrom":[subQ1,subQ0]});Q158=makeQuery(id+"F2.imprint","IMPRINT",FACE,{"disambiguationData":[TD([[makeQuery(id+"F2.imprint","IMPRINT",EDGE,{"disambiguationData":[TD([[subQ2,1.0]])],"derivedFrom":subQ1}),1.0]])]});}
            var Q159;
            {var subQ0=sQuery(id+"F2.wireOp",EDGE,"E67.MirrorCS");var subQ1=sQuery(id+"F2.wireOp",EDGE,"E40.MirrorCS");var subQ2=makeQuery(id+"F2.imprint","INTERSECT",VERTEX,{"derivedFrom":[subQ1,subQ0]});Q159=makeQuery(id+"F2.imprint","IMPRINT",FACE,{"disambiguationData":[TD([[makeQuery(id+"F2.imprint","IMPRINT",EDGE,{"disambiguationData":[TD([[subQ2,-1.0]])],"derivedFrom":subQ1}),1.0]])]});}
            var Q160;
            {var subQ0=sQuery(id+"F2.wireOp",EDGE,"E105.MirrorCS");var subQ1=sQuery(id+"F2.wireOp",EDGE,"E71.MirrorCS");var subQ2=makeQuery(id+"F2.imprint","INTERSECT",VERTEX,{"derivedFrom":[subQ1,subQ0]});Q160=makeQuery(id+"F2.imprint","IMPRINT",FACE,{"disambiguationData":[TD([[makeQuery(id+"F2.imprint","IMPRINT",EDGE,{"disambiguationData":[TD([[subQ2,-1.0]])],"derivedFrom":subQ1}),-1.0]])]});}
            var Q161;
            {var subQ0=sQuery(id+"F2.wireOp",EDGE,"E89.MirrorCS");var subQ1=sQuery(id+"F2.wireOp",EDGE,"E71.MirrorCS");var subQ2=makeQuery(id+"F2.imprint","INTERSECT",VERTEX,{"derivedFrom":[subQ1,subQ0]});Q161=makeQuery(id+"F2.imprint","IMPRINT",FACE,{"disambiguationData":[TD([[makeQuery(id+"F2.imprint","IMPRINT",EDGE,{"disambiguationData":[TD([[subQ2,-1.0]])],"derivedFrom":subQ1}),-1.0]])]});}
            var Q162;
            {var subQ0=sQuery(id+"F2.wireOp",EDGE,"E103.MirrorCS");var subQ1=sQuery(id+"F2.wireOp",EDGE,"E58.MirrorCS");var subQ2=makeQuery(id+"F2.imprint","INTERSECT",VERTEX,{"derivedFrom":[subQ1,subQ0]});Q162=makeQuery(id+"F2.imprint","IMPRINT",FACE,{"disambiguationData":[TD([[makeQuery(id+"F2.imprint","IMPRINT",EDGE,{"disambiguationData":[TD([[subQ2,-1.0]])],"derivedFrom":subQ1}),-1.0]])]});}
            var Q163;
            {var subQ0=sQuery(id+"F2.wireOp",EDGE,"E61.MirrorCS");var subQ1=sQuery(id+"F2.wireOp",EDGE,"E53.MirrorCS");var subQ2=makeQuery(id+"F2.imprint","INTERSECT",VERTEX,{"derivedFrom":[subQ1,subQ0]});Q163=makeQuery(id+"F2.imprint","IMPRINT",FACE,{"disambiguationData":[TD([[makeQuery(id+"F2.imprint","IMPRINT",EDGE,{"disambiguationData":[TD([[subQ2,-1.0]])],"derivedFrom":subQ1}),-1.0]])]});}
            var Q164;
            {var subQ0=sQuery(id+"F2.wireOp",EDGE,"E95.MirrorCS");var subQ1=sQuery(id+"F2.wireOp",EDGE,"E40.MirrorCS");var subQ2=makeQuery(id+"F2.imprint","INTERSECT",VERTEX,{"derivedFrom":[subQ1,subQ0]});Q164=makeQuery(id+"F2.imprint","IMPRINT",FACE,{"disambiguationData":[TD([[makeQuery(id+"F2.imprint","IMPRINT",EDGE,{"disambiguationData":[TD([[subQ2,-1.0]])],"derivedFrom":subQ1}),1.0]])]});}
            var Q165;
            {var subQ0=sQuery(id+"F2.wireOp",EDGE,"E67.MirrorCS");var subQ1=sQuery(id+"F2.wireOp",EDGE,"E54.MirrorCS");var subQ2=makeQuery(id+"F2.imprint","INTERSECT",VERTEX,{"derivedFrom":[subQ1,subQ0]});Q165=makeQuery(id+"F2.imprint","IMPRINT",FACE,{"disambiguationData":[TD([[makeQuery(id+"F2.imprint","IMPRINT",EDGE,{"disambiguationData":[TD([[subQ2,1.0]])],"derivedFrom":subQ1}),-1.0]])]});}
            var Q166;
            {var subQ7=sQuery(id+"F2.wireOp",EDGE,"E36.MirrorCS");var subQ9=sQuery(id+"F2.wireOp",EDGE,"E58.MirrorCS");var subQ10=makeQuery(id+"F2.imprint","INTERSECT",VERTEX,{"derivedFrom":[subQ7,subQ9]});Q166=makeQuery(id+"F2.imprint","IMPRINT",FACE,{"disambiguationData":[TD([[makeQuery(id+"F2.imprint","IMPRINT",EDGE,{"disambiguationData":[TD([[subQ10,1.0]])],"derivedFrom":subQ7}),-1.0]])]});}
            var Q167;
            {var subQ0=sQuery(id+"F2.wireOp",EDGE,"E79.MirrorCS");var subQ1=sQuery(id+"F2.wireOp",EDGE,"E40.MirrorCS");var subQ2=makeQuery(id+"F2.imprint","INTERSECT",VERTEX,{"derivedFrom":[subQ1,subQ0]});Q167=makeQuery(id+"F2.imprint","IMPRINT",FACE,{"disambiguationData":[TD([[makeQuery(id+"F2.imprint","IMPRINT",EDGE,{"disambiguationData":[TD([[subQ2,-1.0]])],"derivedFrom":subQ1}),1.0]])]});}
            var Q168;
            {var subQ3=sQuery(id+"F2.wireOp",EDGE,"E93.MirrorCS");var subQ6=sQuery(id+"F2.wireOp",EDGE,"E36.MirrorCS");var subQ12=makeQuery(id+"F2.imprint","INTERSECT",VERTEX,{"derivedFrom":[subQ6,subQ3]});Q168=makeQuery(id+"F2.imprint","IMPRINT",FACE,{"disambiguationData":[TD([[makeQuery(id+"F2.imprint","IMPRINT",EDGE,{"disambiguationData":[TD([[subQ12,-1.0]])],"derivedFrom":subQ6}),1.0]])]});}
            var Q169;
            {var subQ0=sQuery(id+"F2.wireOp",EDGE,"E100.MirrorCS");var subQ1=sQuery(id+"F2.wireOp",EDGE,"E57.MirrorCS");var subQ2=makeQuery(id+"F2.imprint","INTERSECT",VERTEX,{"derivedFrom":[subQ1,subQ0]});Q169=makeQuery(id+"F2.imprint","IMPRINT",FACE,{"disambiguationData":[TD([[makeQuery(id+"F2.imprint","IMPRINT",EDGE,{"disambiguationData":[TD([[subQ2,-1.0]])],"derivedFrom":subQ1}),-1.0]])]});}
            var Q170;
            {var subQ3=sQuery(id+"F2.wireOp",EDGE,"E77.MirrorCS");var subQ6=sQuery(id+"F2.wireOp",EDGE,"E38.MirrorCS");var subQ12=makeQuery(id+"F2.imprint","INTERSECT",VERTEX,{"derivedFrom":[subQ6,subQ3]});Q170=makeQuery(id+"F2.imprint","IMPRINT",FACE,{"disambiguationData":[TD([[makeQuery(id+"F2.imprint","IMPRINT",EDGE,{"disambiguationData":[TD([[subQ12,-1.0]])],"derivedFrom":subQ6}),1.0]])]});}
            var Q171;
            {var subQ0=sQuery(id+"F2.wireOp",EDGE,"E93.MirrorCS");var subQ1=sQuery(id+"F2.wireOp",EDGE,"E58.MirrorCS");var subQ2=makeQuery(id+"F2.imprint","INTERSECT",VERTEX,{"derivedFrom":[subQ1,subQ0]});Q171=makeQuery(id+"F2.imprint","IMPRINT",FACE,{"disambiguationData":[TD([[makeQuery(id+"F2.imprint","IMPRINT",EDGE,{"disambiguationData":[TD([[subQ2,-1.0]])],"derivedFrom":subQ1}),1.0]])]});}
            var Q172;
            {var subQ0=sQuery(id+"F2.wireOp",EDGE,"E71.MirrorCS");var subQ1=sQuery(id+"F2.wireOp",EDGE,"E35.MirrorCS");var subQ2=makeQuery(id+"F2.imprint","INTERSECT",VERTEX,{"derivedFrom":[subQ1,subQ0]});Q172=makeQuery(id+"F2.imprint","IMPRINT",FACE,{"disambiguationData":[TD([[makeQuery(id+"F2.imprint","IMPRINT",EDGE,{"disambiguationData":[TD([[subQ2,1.0]])],"derivedFrom":subQ1}),-1.0]])]});}
            var Q173;
            {var subQ0=sQuery(id+"F2.wireOp",EDGE,"E93.MirrorCS");var subQ1=sQuery(id+"F2.wireOp",EDGE,"E58.MirrorCS");var subQ2=makeQuery(id+"F2.imprint","INTERSECT",VERTEX,{"derivedFrom":[subQ1,subQ0]});Q173=makeQuery(id+"F2.imprint","IMPRINT",FACE,{"disambiguationData":[TD([[makeQuery(id+"F2.imprint","IMPRINT",EDGE,{"disambiguationData":[TD([[subQ2,-1.0]])],"derivedFrom":subQ1}),-1.0]])]});}
            var Q174;
            {var subQ7=sQuery(id+"F2.wireOp",EDGE,"E87.MirrorCS");var subQ10=sQuery(id+"F2.wireOp",EDGE,"E42.MirrorCS");var subQ11=makeQuery(id+"F2.imprint","INTERSECT",VERTEX,{"derivedFrom":[subQ10,subQ7]});Q174=makeQuery(id+"F2.imprint","IMPRINT",FACE,{"disambiguationData":[TD([[makeQuery(id+"F2.imprint","IMPRINT",EDGE,{"disambiguationData":[TD([[subQ11,1.0]])],"derivedFrom":subQ10}),-1.0]])]});}
            var Q175;
            {var subQ3=sQuery(id+"F2.wireOp",EDGE,"E90.MirrorCS");var subQ9=sQuery(id+"F2.wireOp",EDGE,"E43.MirrorCS");var subQ11=makeQuery(id+"F2.imprint","INTERSECT",VERTEX,{"derivedFrom":[subQ9,subQ3]});Q175=makeQuery(id+"F2.imprint","IMPRINT",FACE,{"disambiguationData":[TD([[makeQuery(id+"F2.imprint","IMPRINT",EDGE,{"disambiguationData":[TD([[subQ11,1.0]])],"derivedFrom":subQ9}),-1.0]])]});}
            var Q176;
            {var subQ0=sQuery(id+"F2.wireOp",EDGE,"E77.MirrorCS");var subQ1=sQuery(id+"F2.wireOp",EDGE,"E58.MirrorCS");var subQ2=makeQuery(id+"F2.imprint","INTERSECT",VERTEX,{"derivedFrom":[subQ1,subQ0]});Q176=makeQuery(id+"F2.imprint","IMPRINT",FACE,{"disambiguationData":[TD([[makeQuery(id+"F2.imprint","IMPRINT",EDGE,{"disambiguationData":[TD([[subQ2,1.0]])],"derivedFrom":subQ1}),1.0]])]});}
            var Q177;
            {var subQ5=sQuery(id+"F2.wireOp",EDGE,"E60.MirrorCS");var subQ6=sQuery(id+"F2.wireOp",EDGE,"E44.MirrorCS");var subQ7=makeQuery(id+"F2.imprint","INTERSECT",VERTEX,{"derivedFrom":[subQ6,subQ5]});Q177=makeQuery(id+"F2.imprint","IMPRINT",FACE,{"disambiguationData":[TD([[makeQuery(id+"F2.imprint","IMPRINT",EDGE,{"disambiguationData":[TD([[subQ7,1.0]])],"derivedFrom":subQ6}),-1.0]])]});}
            var Q178;
            {var subQ0=sQuery(id+"F2.wireOp",EDGE,"E89.MirrorCS");var subQ1=sQuery(id+"F2.wireOp",EDGE,"E60.MirrorCS");var subQ2=makeQuery(id+"F2.imprint","INTERSECT",VERTEX,{"derivedFrom":[subQ1,subQ0]});Q178=makeQuery(id+"F2.imprint","IMPRINT",FACE,{"disambiguationData":[TD([[makeQuery(id+"F2.imprint","IMPRINT",EDGE,{"disambiguationData":[TD([[subQ2,1.0]])],"derivedFrom":subQ1}),1.0]])]});}
            var Q179;
            {var subQ3=sQuery(id+"F2.wireOp",EDGE,"E85.MirrorCS");var subQ6=sQuery(id+"F2.wireOp",EDGE,"E45.MirrorCS");var subQ11=makeQuery(id+"F2.imprint","INTERSECT",VERTEX,{"derivedFrom":[subQ6,subQ3]});Q179=makeQuery(id+"F2.imprint","IMPRINT",FACE,{"disambiguationData":[TD([[makeQuery(id+"F2.imprint","IMPRINT",EDGE,{"disambiguationData":[TD([[subQ11,-1.0]])],"derivedFrom":subQ6}),1.0]])]});}
            var Q180;
            {var subQ8=sQuery(id+"F2.wireOp",EDGE,"E57.MirrorCS");var subQ9=sQuery(id+"F2.wireOp",EDGE,"E38.MirrorCS");var subQ10=makeQuery(id+"F2.imprint","INTERSECT",VERTEX,{"derivedFrom":[subQ9,subQ8]});Q180=makeQuery(id+"F2.imprint","IMPRINT",FACE,{"disambiguationData":[TD([[makeQuery(id+"F2.imprint","IMPRINT",EDGE,{"disambiguationData":[TD([[subQ10,1.0]])],"derivedFrom":subQ9}),-1.0]])]});}
            var Q181;
            {var subQ0=sQuery(id+"F2.wireOp",EDGE,"E89.MirrorCS");var subQ1=sQuery(id+"F2.wireOp",EDGE,"E60.MirrorCS");var subQ2=makeQuery(id+"F2.imprint","INTERSECT",VERTEX,{"derivedFrom":[subQ1,subQ0]});Q181=makeQuery(id+"F2.imprint","IMPRINT",FACE,{"disambiguationData":[TD([[makeQuery(id+"F2.imprint","IMPRINT",EDGE,{"disambiguationData":[TD([[subQ2,1.0]])],"derivedFrom":subQ1}),-1.0]])]});}
            var Q182;
            {var subQ0=sQuery(id+"F2.wireOp",EDGE,"E63.MirrorCS");var subQ1=sQuery(id+"F2.wireOp",EDGE,"E55.MirrorCS");var subQ2=makeQuery(id+"F2.imprint","INTERSECT",VERTEX,{"derivedFrom":[subQ1,subQ0]});Q182=makeQuery(id+"F2.imprint","IMPRINT",FACE,{"disambiguationData":[TD([[makeQuery(id+"F2.imprint","IMPRINT",EDGE,{"disambiguationData":[TD([[subQ2,-1.0]])],"derivedFrom":subQ1}),-1.0]])]});}
            var Q183;
            {var subQ0=sQuery(id+"F2.wireOp",EDGE,"E72.MirrorCS");var subQ1=sQuery(id+"F2.wireOp",EDGE,"E66.MirrorCS");var subQ2=makeQuery(id+"F2.imprint","INTERSECT",VERTEX,{"derivedFrom":[subQ1,subQ0]});Q183=makeQuery(id+"F2.imprint","IMPRINT",FACE,{"disambiguationData":[TD([[makeQuery(id+"F2.imprint","IMPRINT",EDGE,{"disambiguationData":[TD([[subQ2,-1.0]])],"derivedFrom":subQ1}),-1.0]])]});}
            var Q184;
            {var subQ0=sQuery(id+"F2.wireOp",EDGE,"E60.MirrorCS");var subQ1=sQuery(id+"F2.wireOp",EDGE,"E55.MirrorCS");var subQ2=makeQuery(id+"F2.imprint","INTERSECT",VERTEX,{"derivedFrom":[subQ1,subQ0]});Q184=makeQuery(id+"F2.imprint","IMPRINT",FACE,{"disambiguationData":[TD([[makeQuery(id+"F2.imprint","IMPRINT",EDGE,{"disambiguationData":[TD([[subQ2,-1.0]])],"derivedFrom":subQ1}),-1.0]])]});}
            var Q185;
            {var subQ0=sQuery(id+"F2.wireOp",EDGE,"E87.MirrorCS");var subQ1=sQuery(id+"F2.wireOp",EDGE,"E66.MirrorCS");var subQ2=makeQuery(id+"F2.imprint","INTERSECT",VERTEX,{"derivedFrom":[subQ1,subQ0]});Q185=makeQuery(id+"F2.imprint","IMPRINT",FACE,{"disambiguationData":[TD([[makeQuery(id+"F2.imprint","IMPRINT",EDGE,{"disambiguationData":[TD([[subQ2,-1.0]])],"derivedFrom":subQ1}),-1.0]])]});}
            var Q186;
            {var subQ0=sQuery(id+"F2.wireOp",EDGE,"E87.MirrorCS");var subQ1=sQuery(id+"F2.wireOp",EDGE,"E56.MirrorCS");var subQ2=makeQuery(id+"F2.imprint","INTERSECT",VERTEX,{"derivedFrom":[subQ1,subQ0]});Q186=makeQuery(id+"F2.imprint","IMPRINT",FACE,{"disambiguationData":[TD([[makeQuery(id+"F2.imprint","IMPRINT",EDGE,{"disambiguationData":[TD([[subQ2,-1.0]])],"derivedFrom":subQ1}),1.0]])]});}
            var Q187;
            {var subQ0=sQuery(id+"F2.wireOp",EDGE,"E89.MirrorCS");var subQ10=sQuery(id+"F2.wireOp",EDGE,"E35.MirrorCS");var subQ11=makeQuery(id+"F2.imprint","INTERSECT",VERTEX,{"derivedFrom":[subQ10,subQ0]});Q187=makeQuery(id+"F2.imprint","IMPRINT",FACE,{"disambiguationData":[TD([[makeQuery(id+"F2.imprint","IMPRINT",EDGE,{"disambiguationData":[TD([[subQ11,-1.0]])],"derivedFrom":subQ10}),1.0]])]});}
            var Q188;
            {var subQ0=sQuery(id+"F2.wireOp",EDGE,"E95.MirrorCS");var subQ1=sQuery(id+"F2.wireOp",EDGE,"E40.MirrorCS");var subQ2=makeQuery(id+"F2.imprint","INTERSECT",VERTEX,{"derivedFrom":[subQ1,subQ0]});Q188=makeQuery(id+"F2.imprint","IMPRINT",FACE,{"disambiguationData":[TD([[makeQuery(id+"F2.imprint","IMPRINT",EDGE,{"disambiguationData":[TD([[subQ2,-1.0]])],"derivedFrom":subQ1}),-1.0]])]});}
            var Q189;
            {var subQ0=sQuery(id+"F2.wireOp",EDGE,"E96.MirrorCS");var subQ1=sQuery(id+"F2.wireOp",EDGE,"E56.MirrorCS");var subQ2=makeQuery(id+"F2.imprint","INTERSECT",VERTEX,{"derivedFrom":[subQ1,subQ0]});Q189=makeQuery(id+"F2.imprint","IMPRINT",FACE,{"disambiguationData":[TD([[makeQuery(id+"F2.imprint","IMPRINT",EDGE,{"disambiguationData":[TD([[subQ2,-1.0]])],"derivedFrom":subQ1}),1.0]])]});}
            var Q190;
            {var subQ1=sQuery(id+"F2.wireOp",EDGE,"E54.MirrorCS");var subQ10=sQuery(id+"F2.wireOp",EDGE,"E40.MirrorCS");var subQ11=makeQuery(id+"F2.imprint","INTERSECT",VERTEX,{"derivedFrom":[subQ10,subQ1]});Q190=makeQuery(id+"F2.imprint","IMPRINT",FACE,{"disambiguationData":[TD([[makeQuery(id+"F2.imprint","IMPRINT",EDGE,{"disambiguationData":[TD([[subQ11,1.0]])],"derivedFrom":subQ10}),-1.0]])]});}
            var Q191;
            {var subQ0=sQuery(id+"F2.wireOp",EDGE,"E66.MirrorCS");var subQ1=sQuery(id+"F2.wireOp",EDGE,"E42.MirrorCS");var subQ2=makeQuery(id+"F2.imprint","INTERSECT",VERTEX,{"derivedFrom":[subQ1,subQ0]});Q191=makeQuery(id+"F2.imprint","IMPRINT",FACE,{"disambiguationData":[TD([[makeQuery(id+"F2.imprint","IMPRINT",EDGE,{"disambiguationData":[TD([[subQ2,-1.0]])],"derivedFrom":subQ1}),1.0]])]});}
            var Q192;
            {var subQ0=sQuery(id+"F2.wireOp",EDGE,"E71.MirrorCS");var subQ1=sQuery(id+"F2.wireOp",EDGE,"E35.MirrorCS");var subQ2=makeQuery(id+"F2.imprint","INTERSECT",VERTEX,{"derivedFrom":[subQ1,subQ0]});Q192=makeQuery(id+"F2.imprint","IMPRINT",FACE,{"disambiguationData":[TD([[makeQuery(id+"F2.imprint","IMPRINT",EDGE,{"disambiguationData":[TD([[subQ2,1.0]])],"derivedFrom":subQ1}),1.0]])]});}
            var Q193;
            {var subQ0=sQuery(id+"F2.wireOp",EDGE,"E79.MirrorCS");var subQ1=sQuery(id+"F2.wireOp",EDGE,"E40.MirrorCS");var subQ2=makeQuery(id+"F2.imprint","INTERSECT",VERTEX,{"derivedFrom":[subQ1,subQ0]});Q193=makeQuery(id+"F2.imprint","IMPRINT",FACE,{"disambiguationData":[TD([[makeQuery(id+"F2.imprint","IMPRINT",EDGE,{"disambiguationData":[TD([[subQ2,-1.0]])],"derivedFrom":subQ1}),-1.0]])]});}
            var Q194;
            {var subQ0=sQuery(id+"F2.wireOp",EDGE,"E56.MirrorCS");var subQ1=sQuery(id+"F2.wireOp",EDGE,"E45.MirrorCS");var subQ2=makeQuery(id+"F2.imprint","INTERSECT",VERTEX,{"derivedFrom":[subQ1,subQ0]});Q194=makeQuery(id+"F2.imprint","IMPRINT",FACE,{"disambiguationData":[TD([[makeQuery(id+"F2.imprint","IMPRINT",EDGE,{"disambiguationData":[TD([[subQ2,-1.0]])],"derivedFrom":subQ1}),1.0]])]});}
            var Q195;
            {var subQ0=sQuery(id+"F2.wireOp",EDGE,"E74.MirrorCS");var subQ1=sQuery(id+"F2.wireOp",EDGE,"E52.MirrorCS");var subQ2=makeQuery(id+"F2.imprint","INTERSECT",VERTEX,{"derivedFrom":[subQ1,subQ0]});Q195=makeQuery(id+"F2.imprint","IMPRINT",FACE,{"disambiguationData":[TD([[makeQuery(id+"F2.imprint","IMPRINT",EDGE,{"disambiguationData":[TD([[subQ2,1.0]])],"derivedFrom":subQ1}),1.0]])]});}
            var Q196;
            {var subQ0=sQuery(id+"F2.wireOp",EDGE,"E93.MirrorCS");var subQ1=sQuery(id+"F2.wireOp",EDGE,"E35.MirrorCS");var subQ2=makeQuery(id+"F2.imprint","INTERSECT",VERTEX,{"derivedFrom":[subQ1,subQ0]});Q196=makeQuery(id+"F2.imprint","IMPRINT",FACE,{"disambiguationData":[TD([[makeQuery(id+"F2.imprint","IMPRINT",EDGE,{"disambiguationData":[TD([[subQ2,-1.0]])],"derivedFrom":subQ1}),1.0]])]});}
            var Q197;
            {var subQ0=sQuery(id+"F2.wireOp",EDGE,"E79.MirrorCS");var subQ1=sQuery(id+"F2.wireOp",EDGE,"E42.MirrorCS");var subQ2=makeQuery(id+"F2.imprint","INTERSECT",VERTEX,{"derivedFrom":[subQ1,subQ0]});Q197=makeQuery(id+"F2.imprint","IMPRINT",FACE,{"disambiguationData":[TD([[makeQuery(id+"F2.imprint","IMPRINT",EDGE,{"disambiguationData":[TD([[subQ2,-1.0]])],"derivedFrom":subQ1}),1.0]])]});}
            var Q198;
            {var subQ0=sQuery(id+"F2.wireOp",EDGE,"E102.MirrorCS");var subQ1=sQuery(id+"F2.wireOp",EDGE,"E41.MirrorCS");var subQ2=makeQuery(id+"F2.imprint","INTERSECT",VERTEX,{"derivedFrom":[subQ1,subQ0]});Q198=makeQuery(id+"F2.imprint","IMPRINT",FACE,{"disambiguationData":[TD([[makeQuery(id+"F2.imprint","IMPRINT",EDGE,{"disambiguationData":[TD([[subQ2,-1.0]])],"derivedFrom":subQ1}),-1.0]])]});}
            var Q199;
            {var subQ0=sQuery(id+"F2.wireOp",EDGE,"E103.MirrorCS");var subQ1=sQuery(id+"F2.wireOp",EDGE,"E35.MirrorCS");var subQ2=makeQuery(id+"F2.imprint","INTERSECT",VERTEX,{"derivedFrom":[subQ1,subQ0]});Q199=makeQuery(id+"F2.imprint","IMPRINT",FACE,{"disambiguationData":[TD([[makeQuery(id+"F2.imprint","IMPRINT",EDGE,{"disambiguationData":[TD([[subQ2,-1.0]])],"derivedFrom":subQ1}),1.0]])]});}
            var Q200;
            {var subQ0=sQuery(id+"F2.wireOp",EDGE,"E56.MirrorCS");var subQ1=sQuery(id+"F2.wireOp",EDGE,"E42.MirrorCS");var subQ2=makeQuery(id+"F2.imprint","INTERSECT",VERTEX,{"derivedFrom":[subQ1,subQ0]});Q200=makeQuery(id+"F2.imprint","IMPRINT",FACE,{"disambiguationData":[TD([[makeQuery(id+"F2.imprint","IMPRINT",EDGE,{"disambiguationData":[TD([[subQ2,-1.0]])],"derivedFrom":subQ1}),-1.0]])]});}
            var Q201;
            {var subQ0=sQuery(id+"F2.wireOp",EDGE,"E90.MirrorCS");var subQ1=sQuery(id+"F2.wireOp",EDGE,"E43.MirrorCS");var subQ2=makeQuery(id+"F2.imprint","INTERSECT",VERTEX,{"derivedFrom":[subQ1,subQ0]});Q201=makeQuery(id+"F2.imprint","IMPRINT",FACE,{"disambiguationData":[TD([[makeQuery(id+"F2.imprint","IMPRINT",EDGE,{"disambiguationData":[TD([[subQ2,1.0]])],"derivedFrom":subQ1}),1.0]])]});}
            var Q202;
            {var subQ0=sQuery(id+"F2.wireOp",EDGE,"E59.MirrorCS");var subQ1=sQuery(id+"F2.wireOp",EDGE,"E49.MirrorCS");var subQ2=makeQuery(id+"F2.imprint","INTERSECT",VERTEX,{"derivedFrom":[subQ1,subQ0]});Q202=makeQuery(id+"F2.imprint","IMPRINT",FACE,{"disambiguationData":[TD([[makeQuery(id+"F2.imprint","IMPRINT",EDGE,{"disambiguationData":[TD([[subQ2,1.0]])],"derivedFrom":subQ1}),1.0]])]});}
            var Q203;
            {var subQ0=sQuery(id+"F2.wireOp",EDGE,"E54.MirrorCS");var subQ1=sQuery(id+"F2.wireOp",EDGE,"E40.MirrorCS");var subQ2=makeQuery(id+"F2.imprint","INTERSECT",VERTEX,{"derivedFrom":[subQ1,subQ0]});Q203=makeQuery(id+"F2.imprint","IMPRINT",FACE,{"disambiguationData":[TD([[makeQuery(id+"F2.imprint","IMPRINT",EDGE,{"disambiguationData":[TD([[subQ2,1.0]])],"derivedFrom":subQ1}),1.0]])]});}
            var Q204;
            {var subQ0=sQuery(id+"F2.wireOp",EDGE,"E89.MirrorCS");var subQ1=sQuery(id+"F2.wireOp",EDGE,"E44.MirrorCS");var subQ2=makeQuery(id+"F2.imprint","INTERSECT",VERTEX,{"derivedFrom":[subQ1,subQ0]});Q204=makeQuery(id+"F2.imprint","IMPRINT",FACE,{"disambiguationData":[TD([[makeQuery(id+"F2.imprint","IMPRINT",EDGE,{"disambiguationData":[TD([[subQ2,-1.0]])],"derivedFrom":subQ1}),-1.0]])]});}
            var Q205;
            {var subQ0=sQuery(id+"F2.wireOp",EDGE,"E106.MirrorCS");var subQ1=sQuery(id+"F2.wireOp",EDGE,"E36.MirrorCS");var subQ2=makeQuery(id+"F2.imprint","INTERSECT",VERTEX,{"derivedFrom":[subQ1,subQ0]});Q205=makeQuery(id+"F2.imprint","IMPRINT",FACE,{"disambiguationData":[TD([[makeQuery(id+"F2.imprint","IMPRINT",EDGE,{"disambiguationData":[TD([[subQ2,-1.0]])],"derivedFrom":subQ1}),1.0]])]});}
            var Q206;
            {var subQ0=sQuery(id+"F2.wireOp",EDGE,"E100.MirrorCS");var subQ1=sQuery(id+"F2.wireOp",EDGE,"E36.MirrorCS");var subQ2=makeQuery(id+"F2.imprint","INTERSECT",VERTEX,{"derivedFrom":[subQ1,subQ0]});Q206=makeQuery(id+"F2.imprint","IMPRINT",FACE,{"disambiguationData":[TD([[makeQuery(id+"F2.imprint","IMPRINT",EDGE,{"disambiguationData":[TD([[subQ2,-1.0]])],"derivedFrom":subQ1}),-1.0]])]});}
            var Q207;
            {var subQ0=sQuery(id+"F2.wireOp",EDGE,"E60.MirrorCS");var subQ1=sQuery(id+"F2.wireOp",EDGE,"E44.MirrorCS");var subQ2=makeQuery(id+"F2.imprint","INTERSECT",VERTEX,{"derivedFrom":[subQ1,subQ0]});Q207=makeQuery(id+"F2.imprint","IMPRINT",FACE,{"disambiguationData":[TD([[makeQuery(id+"F2.imprint","IMPRINT",EDGE,{"disambiguationData":[TD([[subQ2,1.0]])],"derivedFrom":subQ1}),1.0]])]});}
            var Q208;
            {var subQ0=sQuery(id+"F2.wireOp",EDGE,"E100.MirrorCS");var subQ1=sQuery(id+"F2.wireOp",EDGE,"E36.MirrorCS");var subQ2=makeQuery(id+"F2.imprint","INTERSECT",VERTEX,{"derivedFrom":[subQ1,subQ0]});Q208=makeQuery(id+"F2.imprint","IMPRINT",FACE,{"disambiguationData":[TD([[makeQuery(id+"F2.imprint","IMPRINT",EDGE,{"disambiguationData":[TD([[subQ2,-1.0]])],"derivedFrom":subQ1}),1.0]])]});}
            var Q209;
            {var subQ0=sQuery(id+"F2.wireOp",EDGE,"E85.MirrorCS");var subQ1=sQuery(id+"F2.wireOp",EDGE,"E42.MirrorCS");var subQ2=makeQuery(id+"F2.imprint","INTERSECT",VERTEX,{"derivedFrom":[subQ1,subQ0]});Q209=makeQuery(id+"F2.imprint","IMPRINT",FACE,{"disambiguationData":[TD([[makeQuery(id+"F2.imprint","IMPRINT",EDGE,{"disambiguationData":[TD([[subQ2,-1.0]])],"derivedFrom":subQ1}),1.0]])]});}
            var Q210;
            {var subQ0=sQuery(id+"F2.wireOp",EDGE,"E95.MirrorCS");var subQ1=sQuery(id+"F2.wireOp",EDGE,"E45.MirrorCS");var subQ2=makeQuery(id+"F2.imprint","INTERSECT",VERTEX,{"derivedFrom":[subQ1,subQ0]});Q210=makeQuery(id+"F2.imprint","IMPRINT",FACE,{"disambiguationData":[TD([[makeQuery(id+"F2.imprint","IMPRINT",EDGE,{"disambiguationData":[TD([[subQ2,-1.0]])],"derivedFrom":subQ1}),1.0]])]});}
            var Q211;
            {var subQ0=sQuery(id+"F2.wireOp",EDGE,"E58.MirrorCS");var subQ1=sQuery(id+"F2.wireOp",EDGE,"E36.MirrorCS");var subQ2=makeQuery(id+"F2.imprint","INTERSECT",VERTEX,{"derivedFrom":[subQ1,subQ0]});Q211=makeQuery(id+"F2.imprint","IMPRINT",FACE,{"disambiguationData":[TD([[makeQuery(id+"F2.imprint","IMPRINT",EDGE,{"disambiguationData":[TD([[subQ2,1.0]])],"derivedFrom":subQ1}),1.0]])]});}
            var Q212;
            {var subQ0=sQuery(id+"F2.wireOp",EDGE,"E66.MirrorCS");var subQ1=sQuery(id+"F2.wireOp",EDGE,"E38.MirrorCS");var subQ2=makeQuery(id+"F2.imprint","INTERSECT",VERTEX,{"derivedFrom":[subQ1,subQ0]});Q212=makeQuery(id+"F2.imprint","IMPRINT",FACE,{"disambiguationData":[TD([[makeQuery(id+"F2.imprint","IMPRINT",EDGE,{"disambiguationData":[TD([[subQ2,-1.0]])],"derivedFrom":subQ1}),1.0]])]});}
            var Q213;
            {var subQ0=sQuery(id+"F2.wireOp",EDGE,"E96.MirrorCS");var subQ1=sQuery(id+"F2.wireOp",EDGE,"E45.MirrorCS");var subQ2=makeQuery(id+"F2.imprint","INTERSECT",VERTEX,{"derivedFrom":[subQ1,subQ0]});Q213=makeQuery(id+"F2.imprint","IMPRINT",FACE,{"disambiguationData":[TD([[makeQuery(id+"F2.imprint","IMPRINT",EDGE,{"disambiguationData":[TD([[subQ2,1.0]])],"derivedFrom":subQ1}),1.0]])]});}
            var Q214;
            {var subQ0=sQuery(id+"F2.wireOp",EDGE,"E85.MirrorCS");var subQ1=sQuery(id+"F2.wireOp",EDGE,"E38.MirrorCS");var subQ2=makeQuery(id+"F2.imprint","INTERSECT",VERTEX,{"derivedFrom":[subQ1,subQ0]});Q214=makeQuery(id+"F2.imprint","IMPRINT",FACE,{"disambiguationData":[TD([[makeQuery(id+"F2.imprint","IMPRINT",EDGE,{"disambiguationData":[TD([[subQ2,-1.0]])],"derivedFrom":subQ1}),1.0]])]});}
            var Q215;
            {var subQ0=sQuery(id+"F2.wireOp",EDGE,"E66.MirrorCS");var subQ1=sQuery(id+"F2.wireOp",EDGE,"E38.MirrorCS");var subQ2=makeQuery(id+"F2.imprint","INTERSECT",VERTEX,{"derivedFrom":[subQ1,subQ0]});Q215=makeQuery(id+"F2.imprint","IMPRINT",FACE,{"disambiguationData":[TD([[makeQuery(id+"F2.imprint","IMPRINT",EDGE,{"disambiguationData":[TD([[subQ2,-1.0]])],"derivedFrom":subQ1}),-1.0]])]});}
            var Q216;
            {var subQ0=sQuery(id+"F2.wireOp",EDGE,"E86.MirrorCS");var subQ1=sQuery(id+"F2.wireOp",EDGE,"E41.MirrorCS");var subQ2=makeQuery(id+"F2.imprint","INTERSECT",VERTEX,{"derivedFrom":[subQ1,subQ0]});Q216=makeQuery(id+"F2.imprint","IMPRINT",FACE,{"disambiguationData":[TD([[makeQuery(id+"F2.imprint","IMPRINT",EDGE,{"disambiguationData":[TD([[subQ2,-1.0]])],"derivedFrom":subQ1}),-1.0]])]});}
            var Q217;
            {var subQ0=sQuery(id+"F2.wireOp",EDGE,"E105.MirrorCS");var subQ1=sQuery(id+"F2.wireOp",EDGE,"E47.MirrorCS");var subQ2=makeQuery(id+"F2.imprint","INTERSECT",VERTEX,{"derivedFrom":[subQ1,subQ0]});Q217=makeQuery(id+"F2.imprint","IMPRINT",FACE,{"disambiguationData":[TD([[makeQuery(id+"F2.imprint","IMPRINT",EDGE,{"disambiguationData":[TD([[subQ2,-1.0]])],"derivedFrom":subQ1}),-1.0]])]});}
            var Q218;
            {var subQ0=sQuery(id+"F2.wireOp",EDGE,"E57.MirrorCS");var subQ1=sQuery(id+"F2.wireOp",EDGE,"E38.MirrorCS");var subQ2=makeQuery(id+"F2.imprint","INTERSECT",VERTEX,{"derivedFrom":[subQ1,subQ0]});Q218=makeQuery(id+"F2.imprint","IMPRINT",FACE,{"disambiguationData":[TD([[makeQuery(id+"F2.imprint","IMPRINT",EDGE,{"disambiguationData":[TD([[subQ2,1.0]])],"derivedFrom":subQ1}),1.0]])]});}
            var Q219;
            {var subQ0=sQuery(id+"F2.wireOp",EDGE,"E106.MirrorCS");var subQ1=sQuery(id+"F2.wireOp",EDGE,"E38.MirrorCS");var subQ2=makeQuery(id+"F2.imprint","INTERSECT",VERTEX,{"derivedFrom":[subQ1,subQ0]});Q219=makeQuery(id+"F2.imprint","IMPRINT",FACE,{"disambiguationData":[TD([[makeQuery(id+"F2.imprint","IMPRINT",EDGE,{"disambiguationData":[TD([[subQ2,-1.0]])],"derivedFrom":subQ1}),1.0]])]});}
            var Q220;
            {var subQ0=sQuery(id+"F2.wireOp",EDGE,"E63.MirrorCS");var subQ1=sQuery(id+"F2.wireOp",EDGE,"E47.MirrorCS");var subQ2=makeQuery(id+"F2.imprint","INTERSECT",VERTEX,{"derivedFrom":[subQ1,subQ0]});Q220=makeQuery(id+"F2.imprint","IMPRINT",FACE,{"disambiguationData":[TD([[makeQuery(id+"F2.imprint","IMPRINT",EDGE,{"disambiguationData":[TD([[subQ2,1.0]])],"derivedFrom":subQ1}),1.0]])]});}
            var Q221;
            {var subQ0=sQuery(id+"F2.wireOp",EDGE,"E101.MirrorCS");var subQ1=sQuery(id+"F2.wireOp",EDGE,"E39.MirrorCS");var subQ2=makeQuery(id+"F2.imprint","INTERSECT",VERTEX,{"derivedFrom":[subQ1,subQ0]});Q221=makeQuery(id+"F2.imprint","IMPRINT",FACE,{"disambiguationData":[TD([[makeQuery(id+"F2.imprint","IMPRINT",EDGE,{"disambiguationData":[TD([[subQ2,1.0]])],"derivedFrom":subQ1}),1.0]])]});}
            var Q222;
            {var subQ0=sQuery(id+"F2.wireOp",EDGE,"E77.MirrorCS");var subQ1=sQuery(id+"F2.wireOp",EDGE,"E38.MirrorCS");var subQ2=makeQuery(id+"F2.imprint","INTERSECT",VERTEX,{"derivedFrom":[subQ1,subQ0]});Q222=makeQuery(id+"F2.imprint","IMPRINT",FACE,{"disambiguationData":[TD([[makeQuery(id+"F2.imprint","IMPRINT",EDGE,{"disambiguationData":[TD([[subQ2,-1.0]])],"derivedFrom":subQ1}),-1.0]])]});}
            var Q223;
            {var subQ0=sQuery(id+"F2.wireOp",EDGE,"E68.MirrorCS");var subQ1=sQuery(id+"F2.wireOp",EDGE,"E48.MirrorCS");var subQ2=makeQuery(id+"F2.imprint","INTERSECT",VERTEX,{"derivedFrom":[subQ1,subQ0]});Q223=makeQuery(id+"F2.imprint","IMPRINT",FACE,{"disambiguationData":[TD([[makeQuery(id+"F2.imprint","IMPRINT",EDGE,{"disambiguationData":[TD([[subQ2,1.0]])],"derivedFrom":subQ1}),1.0]])]});}
            var Q224;
            {var subQ0=sQuery(id+"F2.wireOp",EDGE,"E67.MirrorCS");var subQ1=sQuery(id+"F2.wireOp",EDGE,"E40.MirrorCS");var subQ2=makeQuery(id+"F2.imprint","INTERSECT",VERTEX,{"derivedFrom":[subQ1,subQ0]});Q224=makeQuery(id+"F2.imprint","IMPRINT",FACE,{"disambiguationData":[TD([[makeQuery(id+"F2.imprint","IMPRINT",EDGE,{"disambiguationData":[TD([[subQ2,-1.0]])],"derivedFrom":subQ1}),-1.0]])]});}
            var Q225;
            {var subQ0=sQuery(id+"F2.wireOp",EDGE,"E55.MirrorCS");var subQ1=sQuery(id+"F2.wireOp",EDGE,"E41.MirrorCS");var subQ2=makeQuery(id+"F2.imprint","INTERSECT",VERTEX,{"derivedFrom":[subQ1,subQ0]});Q225=makeQuery(id+"F2.imprint","IMPRINT",FACE,{"disambiguationData":[TD([[makeQuery(id+"F2.imprint","IMPRINT",EDGE,{"disambiguationData":[TD([[subQ2,-1.0]])],"derivedFrom":subQ1}),1.0]])]});}
            var Q226;
            {var subQ0=sQuery(id+"F2.wireOp",EDGE,"E72.MirrorCS");var subQ1=sQuery(id+"F2.wireOp",EDGE,"E51.MirrorCS");var subQ2=makeQuery(id+"F2.imprint","INTERSECT",VERTEX,{"derivedFrom":[subQ1,subQ0]});Q226=makeQuery(id+"F2.imprint","IMPRINT",FACE,{"disambiguationData":[TD([[makeQuery(id+"F2.imprint","IMPRINT",EDGE,{"disambiguationData":[TD([[subQ2,1.0]])],"derivedFrom":subQ1}),1.0]])]});}
            var Q227;
            {var subQ0=sQuery(id+"F2.wireOp",EDGE,"E55.MirrorCS");var subQ1=sQuery(id+"F2.wireOp",EDGE,"E44.MirrorCS");var subQ2=makeQuery(id+"F2.imprint","INTERSECT",VERTEX,{"derivedFrom":[subQ1,subQ0]});Q227=makeQuery(id+"F2.imprint","IMPRINT",FACE,{"disambiguationData":[TD([[makeQuery(id+"F2.imprint","IMPRINT",EDGE,{"disambiguationData":[TD([[subQ2,-1.0]])],"derivedFrom":subQ1}),-1.0]])]});}
            var Q228;
            {var subQ0=sQuery(id+"F2.wireOp",EDGE,"E103.MirrorCS");var subQ1=sQuery(id+"F2.wireOp",EDGE,"E43.MirrorCS");var subQ2=makeQuery(id+"F2.imprint","INTERSECT",VERTEX,{"derivedFrom":[subQ1,subQ0]});Q228=makeQuery(id+"F2.imprint","IMPRINT",FACE,{"disambiguationData":[TD([[makeQuery(id+"F2.imprint","IMPRINT",EDGE,{"disambiguationData":[TD([[subQ2,-1.0]])],"derivedFrom":subQ1}),-1.0]])]});}
            var Q229;
            {var subQ0=sQuery(id+"F2.wireOp",EDGE,"E93.MirrorCS");var subQ1=sQuery(id+"F2.wireOp",EDGE,"E35.MirrorCS");var subQ2=makeQuery(id+"F2.imprint","INTERSECT",VERTEX,{"derivedFrom":[subQ1,subQ0]});Q229=makeQuery(id+"F2.imprint","IMPRINT",FACE,{"disambiguationData":[TD([[makeQuery(id+"F2.imprint","IMPRINT",EDGE,{"disambiguationData":[TD([[subQ2,-1.0]])],"derivedFrom":subQ1}),-1.0]])]});}
            var Q230;
            {var subQ0=sQuery(id+"F2.wireOp",EDGE,"E89.MirrorCS");var subQ1=sQuery(id+"F2.wireOp",EDGE,"E35.MirrorCS");var subQ2=makeQuery(id+"F2.imprint","INTERSECT",VERTEX,{"derivedFrom":[subQ1,subQ0]});Q230=makeQuery(id+"F2.imprint","IMPRINT",FACE,{"disambiguationData":[TD([[makeQuery(id+"F2.imprint","IMPRINT",EDGE,{"disambiguationData":[TD([[subQ2,-1.0]])],"derivedFrom":subQ1}),-1.0]])]});}
            var Q231;
            {var subQ0=sQuery(id+"F2.wireOp",EDGE,"E86.MirrorCS");var subQ1=sQuery(id+"F2.wireOp",EDGE,"E41.MirrorCS");var subQ2=makeQuery(id+"F2.imprint","INTERSECT",VERTEX,{"derivedFrom":[subQ1,subQ0]});Q231=makeQuery(id+"F2.imprint","IMPRINT",FACE,{"disambiguationData":[TD([[makeQuery(id+"F2.imprint","IMPRINT",EDGE,{"disambiguationData":[TD([[subQ2,-1.0]])],"derivedFrom":subQ1}),1.0]])]});}
            var Q232;
            {var subQ0=sQuery(id+"F2.wireOp",EDGE,"E77.MirrorCS");var subQ1=sQuery(id+"F2.wireOp",EDGE,"E36.MirrorCS");var subQ2=makeQuery(id+"F2.imprint","INTERSECT",VERTEX,{"derivedFrom":[subQ1,subQ0]});Q232=makeQuery(id+"F2.imprint","IMPRINT",FACE,{"disambiguationData":[TD([[makeQuery(id+"F2.imprint","IMPRINT",EDGE,{"disambiguationData":[TD([[subQ2,-1.0]])],"derivedFrom":subQ1}),1.0]])]});}
            var Q233;
            {var subQ0=sQuery(id+"F2.wireOp",EDGE,"E103.MirrorCS");var subQ1=sQuery(id+"F2.wireOp",EDGE,"E35.MirrorCS");var subQ2=makeQuery(id+"F2.imprint","INTERSECT",VERTEX,{"derivedFrom":[subQ1,subQ0]});Q233=makeQuery(id+"F2.imprint","IMPRINT",FACE,{"disambiguationData":[TD([[makeQuery(id+"F2.imprint","IMPRINT",EDGE,{"disambiguationData":[TD([[subQ2,-1.0]])],"derivedFrom":subQ1}),-1.0]])]});}
            var Q234;
            {var subQ0=sQuery(id+"F2.wireOp",EDGE,"E100.MirrorCS");var subQ1=sQuery(id+"F2.wireOp",EDGE,"E35.MirrorCS");var subQ2=makeQuery(id+"F2.imprint","INTERSECT",VERTEX,{"derivedFrom":[subQ1,subQ0]});Q234=makeQuery(id+"F2.imprint","IMPRINT",FACE,{"disambiguationData":[TD([[makeQuery(id+"F2.imprint","IMPRINT",EDGE,{"disambiguationData":[TD([[subQ2,-1.0]])],"derivedFrom":subQ1}),1.0]])]});}
            var Q235;
            {var subQ0=sQuery(id+"F2.wireOp",EDGE,"E87.MirrorCS");var subQ1=sQuery(id+"F2.wireOp",EDGE,"E42.MirrorCS");var subQ2=makeQuery(id+"F2.imprint","INTERSECT",VERTEX,{"derivedFrom":[subQ1,subQ0]});Q235=makeQuery(id+"F2.imprint","IMPRINT",FACE,{"disambiguationData":[TD([[makeQuery(id+"F2.imprint","IMPRINT",EDGE,{"disambiguationData":[TD([[subQ2,1.0]])],"derivedFrom":subQ1}),1.0]])]});}
            var Q236;
            {var subQ0=sQuery(id+"F2.wireOp",EDGE,"E102.MirrorCS");var subQ1=sQuery(id+"F2.wireOp",EDGE,"E47.MirrorCS");var subQ2=makeQuery(id+"F2.imprint","INTERSECT",VERTEX,{"derivedFrom":[subQ1,subQ0]});Q236=makeQuery(id+"F2.imprint","IMPRINT",FACE,{"disambiguationData":[TD([[makeQuery(id+"F2.imprint","IMPRINT",EDGE,{"disambiguationData":[TD([[subQ2,-1.0]])],"derivedFrom":subQ1}),-1.0]])]});}
            var Q237;
            {var subQ0=sQuery(id+"F2.wireOp",EDGE,"E102.MirrorCS");var subQ1=sQuery(id+"F2.wireOp",EDGE,"E41.MirrorCS");var subQ2=makeQuery(id+"F2.imprint","INTERSECT",VERTEX,{"derivedFrom":[subQ1,subQ0]});Q237=makeQuery(id+"F2.imprint","IMPRINT",FACE,{"disambiguationData":[TD([[makeQuery(id+"F2.imprint","IMPRINT",EDGE,{"disambiguationData":[TD([[subQ2,-1.0]])],"derivedFrom":subQ1}),1.0]])]});}
            var Q238;
            {var subQ0=sQuery(id+"F2.wireOp",EDGE,"E55.MirrorCS");var subQ1=sQuery(id+"F2.wireOp",EDGE,"E47.MirrorCS");var subQ2=makeQuery(id+"F2.imprint","INTERSECT",VERTEX,{"derivedFrom":[subQ1,subQ0]});Q238=makeQuery(id+"F2.imprint","IMPRINT",FACE,{"disambiguationData":[TD([[makeQuery(id+"F2.imprint","IMPRINT",EDGE,{"disambiguationData":[TD([[subQ2,-1.0]])],"derivedFrom":subQ1}),-1.0]])]});}
            var Q239;
            {var subQ0=sQuery(id+"F2.wireOp",EDGE,"E79.MirrorCS");var subQ1=sQuery(id+"F2.wireOp",EDGE,"E45.MirrorCS");var subQ2=makeQuery(id+"F2.imprint","INTERSECT",VERTEX,{"derivedFrom":[subQ1,subQ0]});Q239=makeQuery(id+"F2.imprint","IMPRINT",FACE,{"disambiguationData":[TD([[makeQuery(id+"F2.imprint","IMPRINT",EDGE,{"disambiguationData":[TD([[subQ2,-1.0]])],"derivedFrom":subQ1}),1.0]])]});}
            var Q240;
            {var subQ0=sQuery(id+"F2.wireOp",EDGE,"E77.MirrorCS");var subQ1=sQuery(id+"F2.wireOp",EDGE,"E36.MirrorCS");var subQ2=makeQuery(id+"F2.imprint","INTERSECT",VERTEX,{"derivedFrom":[subQ1,subQ0]});Q240=makeQuery(id+"F2.imprint","IMPRINT",FACE,{"disambiguationData":[TD([[makeQuery(id+"F2.imprint","IMPRINT",EDGE,{"disambiguationData":[TD([[subQ2,-1.0]])],"derivedFrom":subQ1}),-1.0]])]});}
            var Q241;
            {var subQ0=sQuery(id+"F2.wireOp",EDGE,"E56.MirrorCS");var subQ1=sQuery(id+"F2.wireOp",EDGE,"E42.MirrorCS");var subQ2=makeQuery(id+"F2.imprint","INTERSECT",VERTEX,{"derivedFrom":[subQ1,subQ0]});Q241=makeQuery(id+"F2.imprint","IMPRINT",FACE,{"disambiguationData":[TD([[makeQuery(id+"F2.imprint","IMPRINT",EDGE,{"disambiguationData":[TD([[subQ2,-1.0]])],"derivedFrom":subQ1}),1.0]])]});}
            var Q242;
            {var subQ0=sQuery(id+"F2.wireOp",EDGE,"E93.MirrorCS");var subQ1=sQuery(id+"F2.wireOp",EDGE,"E36.MirrorCS");var subQ2=makeQuery(id+"F2.imprint","INTERSECT",VERTEX,{"derivedFrom":[subQ1,subQ0]});Q242=makeQuery(id+"F2.imprint","IMPRINT",FACE,{"disambiguationData":[TD([[makeQuery(id+"F2.imprint","IMPRINT",EDGE,{"disambiguationData":[TD([[subQ2,-1.0]])],"derivedFrom":subQ1}),-1.0]])]});}
            var Q243;
            {var subQ0=sQuery(id+"F2.wireOp",EDGE,"E85.MirrorCS");var subQ1=sQuery(id+"F2.wireOp",EDGE,"E42.MirrorCS");var subQ2=makeQuery(id+"F2.imprint","INTERSECT",VERTEX,{"derivedFrom":[subQ1,subQ0]});Q243=makeQuery(id+"F2.imprint","IMPRINT",FACE,{"disambiguationData":[TD([[makeQuery(id+"F2.imprint","IMPRINT",EDGE,{"disambiguationData":[TD([[subQ2,-1.0]])],"derivedFrom":subQ1}),-1.0]])]});}
            var Q244;
            {var subQ0=sQuery(id+"F2.wireOp",EDGE,"E86.MirrorCS");var subQ1=sQuery(id+"F2.wireOp",EDGE,"E46.MirrorCS");var subQ2=makeQuery(id+"F2.imprint","INTERSECT",VERTEX,{"derivedFrom":[subQ1,subQ0]});Q244=makeQuery(id+"F2.imprint","IMPRINT",FACE,{"disambiguationData":[TD([[makeQuery(id+"F2.imprint","IMPRINT",EDGE,{"disambiguationData":[TD([[subQ2,-1.0]])],"derivedFrom":subQ1}),1.0]])]});}
            var Q245;
            {var subQ0=sQuery(id+"F2.wireOp",EDGE,"E66.MirrorCS");var subQ1=sQuery(id+"F2.wireOp",EDGE,"E42.MirrorCS");var subQ2=makeQuery(id+"F2.imprint","INTERSECT",VERTEX,{"derivedFrom":[subQ1,subQ0]});Q245=makeQuery(id+"F2.imprint","IMPRINT",FACE,{"disambiguationData":[TD([[makeQuery(id+"F2.imprint","IMPRINT",EDGE,{"disambiguationData":[TD([[subQ2,-1.0]])],"derivedFrom":subQ1}),-1.0]])]});}
            var Q246;
            {var subQ0=sQuery(id+"F2.wireOp",EDGE,"E106.MirrorCS");var subQ1=sQuery(id+"F2.wireOp",EDGE,"E38.MirrorCS");var subQ2=makeQuery(id+"F2.imprint","INTERSECT",VERTEX,{"derivedFrom":[subQ1,subQ0]});Q246=makeQuery(id+"F2.imprint","IMPRINT",FACE,{"disambiguationData":[TD([[makeQuery(id+"F2.imprint","IMPRINT",EDGE,{"disambiguationData":[TD([[subQ2,-1.0]])],"derivedFrom":subQ1}),-1.0]])]});}
            var Q247;
            {var subQ0=sQuery(id+"F2.wireOp",EDGE,"E89.MirrorCS");var subQ1=sQuery(id+"F2.wireOp",EDGE,"E43.MirrorCS");var subQ2=makeQuery(id+"F2.imprint","INTERSECT",VERTEX,{"derivedFrom":[subQ1,subQ0]});Q247=makeQuery(id+"F2.imprint","IMPRINT",FACE,{"disambiguationData":[TD([[makeQuery(id+"F2.imprint","IMPRINT",EDGE,{"disambiguationData":[TD([[subQ2,-1.0]])],"derivedFrom":subQ1}),-1.0]])]});}
            var Q248;
            {var subQ0=sQuery(id+"F2.wireOp",EDGE,"E105.MirrorCS");var subQ1=sQuery(id+"F2.wireOp",EDGE,"E43.MirrorCS");var subQ2=makeQuery(id+"F2.imprint","INTERSECT",VERTEX,{"derivedFrom":[subQ1,subQ0]});Q248=makeQuery(id+"F2.imprint","IMPRINT",FACE,{"disambiguationData":[TD([[makeQuery(id+"F2.imprint","IMPRINT",EDGE,{"disambiguationData":[TD([[subQ2,-1.0]])],"derivedFrom":subQ1}),-1.0]])]});}
            var Q249;
            {var subQ0=sQuery(id+"F2.wireOp",EDGE,"E105.MirrorCS");var subQ1=sQuery(id+"F2.wireOp",EDGE,"E44.MirrorCS");var subQ2=makeQuery(id+"F2.imprint","INTERSECT",VERTEX,{"derivedFrom":[subQ1,subQ0]});Q249=makeQuery(id+"F2.imprint","IMPRINT",FACE,{"disambiguationData":[TD([[makeQuery(id+"F2.imprint","IMPRINT",EDGE,{"disambiguationData":[TD([[subQ2,-1.0]])],"derivedFrom":subQ1}),-1.0]])]});}
            extrude(context, id + "F3", {"entities" : qUnion([Q0, Q1, Q2, Q3, Q4, Q5, Q6, Q7, Q8, Q9, Q10, Q11, Q12, Q13, Q14, Q15, Q16, Q17, Q18, Q19, Q20, Q21, Q22, Q23, Q24, Q25, Q26, Q27, Q28, Q29, Q30, Q31, Q32, Q33, Q34, Q35, Q36, Q37, Q38, Q39, Q40, Q41, Q42, Q43, Q44, Q45, Q46, Q47, Q48, Q49, Q50, Q51, Q52, Q53, Q54, Q55, Q56, Q57, Q58, Q59, Q60, Q61, Q62, Q63, Q64, Q65, Q66, Q67, Q68, Q69, Q70, Q71, Q72, Q73, Q74, Q75, Q76, Q77, Q78, Q79, Q80, Q81, Q82, Q83, Q84, Q85, Q86, Q87, Q88, Q89, Q90, Q91, Q92, Q93, Q94, Q95, Q96, Q97, Q98, Q99, Q100, Q101, Q102, Q103, Q104, Q105, Q106, Q107, Q108, Q109, Q110, Q111, Q112, Q113, Q114, Q115, Q116, Q117, Q118, Q119, Q120, Q121, Q122, Q123, Q124, Q125, Q126, Q127, Q128, Q129, Q130, Q131, Q132, Q133, Q134, Q135, Q136, Q137, Q138, Q139, Q140, Q141, Q142, Q143, Q144, Q145, Q146, Q147, Q148, Q149, Q150, Q151, Q152, Q153, Q154, Q155, Q156, Q157, Q158, Q159, Q160, Q161, Q162, Q163, Q164, Q165, Q166, Q167, Q168, Q169, Q170, Q171, Q172, Q173, Q174, Q175, Q176, Q177, Q178, Q179, Q180, Q181, Q182, Q183, Q184, Q185, Q186, Q187, Q188, Q189, Q190, Q191, Q192, Q193, Q194, Q195, Q196, Q197, Q198, Q199, Q200, Q201, Q202, Q203, Q204, Q205, Q206, Q207, Q208, Q209, Q210, Q211, Q212, Q213, Q214, Q215, Q216, Q217, Q218, Q219, Q220, Q221, Q222, Q223, Q224, Q225, Q226, Q227, Q228, Q229, Q230, Q231, Q232, Q233, Q234, Q235, Q236, Q237, Q238, Q239, Q240, Q241, Q242, Q243, Q244, Q245, Q246, Q247, Q248, Q249]), "operationType" : NewBodyOperationType.REMOVE, "oppositeDirection" : true, "depth" : 25 * mm, "symmetric" : true});
        }
        {
            var Q0;
            Q0=makeQuery(id+"F1.opExtrude","CAP_FACE",FACE,{"disambiguationData":[OSD([sQuery(id+"F0.wireOp",EDGE,"E0"),sQuery(id+"F0.wireOp",EDGE,"E1"),sQuery(id+"F0.wireOp",EDGE,"E3.trimOffspring"),sQuery(id+"F0.wireOp",EDGE,"E4.MirrorCS"),sQuery(id+"F0.wireOp",EDGE,"E5.MirrorCS"),sQuery(id+"F0.wireOp",EDGE,"E6.MirrorCS"),sQuery(id+"F0.wireOp",EDGE,"E7.MirrorCS"),sQuery(id+"F0.wireOp",EDGE,"E8.trimOffspring"),sQuery(id+"F0.wireOp",EDGE,"E9.trimOffspring"),sQuery(id+"F0.wireOp",EDGE,"E10"),sQuery(id+"F0.wireOp",EDGE,"E12"),sQuery(id+"F0.wireOp",EDGE,"E14.0"),sQuery(id+"F0.wireOp",EDGE,"E14.2"),sQuery(id+"F0.wireOp",EDGE,"E17.1.1"),sQuery(id+"F0.wireOp",EDGE,"E17.1.2"),sQuery(id+"F0.wireOp",EDGE,"E17.2.1"),sQuery(id+"F0.wireOp",EDGE,"E17.2.2"),sQuery(id+"F0.wireOp",EDGE,"E17.3.1"),sQuery(id+"F0.wireOp",EDGE,"E17.3.2"),sQuery(id+"F0.wireOp",EDGE,"E17.4.1"),sQuery(id+"F0.wireOp",EDGE,"E17.4.2"),sQuery(id+"F0.wireOp",EDGE,"E17.5.1"),sQuery(id+"F0.wireOp",EDGE,"E17.5.2"),sQuery(id+"F0.wireOp",EDGE,"E17.6.1"),sQuery(id+"F0.wireOp",EDGE,"E17.6.2"),sQuery(id+"F0.wireOp",EDGE,"E17.7.1"),sQuery(id+"F0.wireOp",EDGE,"E17.7.2"),sQuery(id+"F0.wireOp",EDGE,"E17.8.1"),sQuery(id+"F0.wireOp",EDGE,"E17.8.2"),sQuery(id+"F0.wireOp",EDGE,"E17.10.1"),sQuery(id+"F0.wireOp",EDGE,"E17.10.2"),sQuery(id+"F0.wireOp",EDGE,"E17.11.1"),sQuery(id+"F0.wireOp",EDGE,"E17.11.2"),sQuery(id+"F0.wireOp",EDGE,"E18.trimOffspring"),sQuery(id+"F0.wireOp",EDGE,"E19.trimOffspring"),sQuery(id+"F0.wireOp",EDGE,"E20.trimOffspring"),sQuery(id+"F0.wireOp",EDGE,"E21.trimOffspring"),sQuery(id+"F0.wireOp",EDGE,"E22.trimOffspring"),sQuery(id+"F0.wireOp",EDGE,"E23.trimOffspring"),sQuery(id+"F0.wireOp",EDGE,"E24.trimOffspring"),sQuery(id+"F0.wireOp",EDGE,"E25.trimOffspring"),sQuery(id+"F0.wireOp",EDGE,"E26.trimOffspring"),sQuery(id+"F0.wireOp",EDGE,"E27.trimOffspring"),sQuery(id+"F0.wireOp",EDGE,"E28.trimOffspring"),sQuery(id+"F0.wireOp",EDGE,"E29"),sQuery(id+"F0.wireOp",EDGE,"E30")])],"isStart":false});
            var Q1;
            {var subQ0=sQuery(id+"F0.wireOp",EDGE,"E29");var subQ1=sQuery(id+"F0.wireOp",EDGE,"E8.trimOffspring");var subQ4=sQuery(id+"F0.wireOp",EDGE,"E1");Q1=makeQuery(id+"F3.boolean.opBoolean","SPLIT",EDGE,{"disambiguationData":[TD([makeQuery(id+"F3.opExtrude","SWEPT_FACE",FACE,{"disambiguationData":[OSD([sQuery(id+"F2.wireOp",EDGE,"E31.0")])]})])],"derivedFrom":makeQuery(id+"F1.opExtrude","CAP_EDGE",EDGE,{"disambiguationData":[OSD([subQ4,subQ1,subQ0])],"isStart":true})});}
            var Q2;
            Q2=makeQuery(id+"F1.opExtrude","CAP_FACE",FACE,{"disambiguationData":[OSD([sQuery(id+"F0.wireOp",EDGE,"E0"),sQuery(id+"F0.wireOp",EDGE,"E1"),sQuery(id+"F0.wireOp",EDGE,"E3.trimOffspring"),sQuery(id+"F0.wireOp",EDGE,"E4.MirrorCS"),sQuery(id+"F0.wireOp",EDGE,"E5.MirrorCS"),sQuery(id+"F0.wireOp",EDGE,"E6.MirrorCS"),sQuery(id+"F0.wireOp",EDGE,"E7.MirrorCS"),sQuery(id+"F0.wireOp",EDGE,"E8.trimOffspring"),sQuery(id+"F0.wireOp",EDGE,"E9.trimOffspring"),sQuery(id+"F0.wireOp",EDGE,"E10"),sQuery(id+"F0.wireOp",EDGE,"E12"),sQuery(id+"F0.wireOp",EDGE,"E14.0"),sQuery(id+"F0.wireOp",EDGE,"E14.2"),sQuery(id+"F0.wireOp",EDGE,"E17.1.1"),sQuery(id+"F0.wireOp",EDGE,"E17.1.2"),sQuery(id+"F0.wireOp",EDGE,"E17.2.1"),sQuery(id+"F0.wireOp",EDGE,"E17.2.2"),sQuery(id+"F0.wireOp",EDGE,"E17.3.1"),sQuery(id+"F0.wireOp",EDGE,"E17.3.2"),sQuery(id+"F0.wireOp",EDGE,"E17.4.1"),sQuery(id+"F0.wireOp",EDGE,"E17.4.2"),sQuery(id+"F0.wireOp",EDGE,"E17.5.1"),sQuery(id+"F0.wireOp",EDGE,"E17.5.2"),sQuery(id+"F0.wireOp",EDGE,"E17.6.1"),sQuery(id+"F0.wireOp",EDGE,"E17.6.2"),sQuery(id+"F0.wireOp",EDGE,"E17.7.1"),sQuery(id+"F0.wireOp",EDGE,"E17.7.2"),sQuery(id+"F0.wireOp",EDGE,"E17.8.1"),sQuery(id+"F0.wireOp",EDGE,"E17.8.2"),sQuery(id+"F0.wireOp",EDGE,"E17.10.1"),sQuery(id+"F0.wireOp",EDGE,"E17.10.2"),sQuery(id+"F0.wireOp",EDGE,"E17.11.1"),sQuery(id+"F0.wireOp",EDGE,"E17.11.2"),sQuery(id+"F0.wireOp",EDGE,"E18.trimOffspring"),sQuery(id+"F0.wireOp",EDGE,"E19.trimOffspring"),sQuery(id+"F0.wireOp",EDGE,"E20.trimOffspring"),sQuery(id+"F0.wireOp",EDGE,"E21.trimOffspring"),sQuery(id+"F0.wireOp",EDGE,"E22.trimOffspring"),sQuery(id+"F0.wireOp",EDGE,"E23.trimOffspring"),sQuery(id+"F0.wireOp",EDGE,"E24.trimOffspring"),sQuery(id+"F0.wireOp",EDGE,"E25.trimOffspring"),sQuery(id+"F0.wireOp",EDGE,"E26.trimOffspring"),sQuery(id+"F0.wireOp",EDGE,"E27.trimOffspring"),sQuery(id+"F0.wireOp",EDGE,"E28.trimOffspring"),sQuery(id+"F0.wireOp",EDGE,"E29"),sQuery(id+"F0.wireOp",EDGE,"E30")])],"isStart":true});
            fillet(context, id + "F4", {"entities" : qUnion([Q0, Q1, Q2]), "radius" : 1 * mm, "tangentPropagation" : true, "allowEdgeOverflow" : false});
        }
    });
